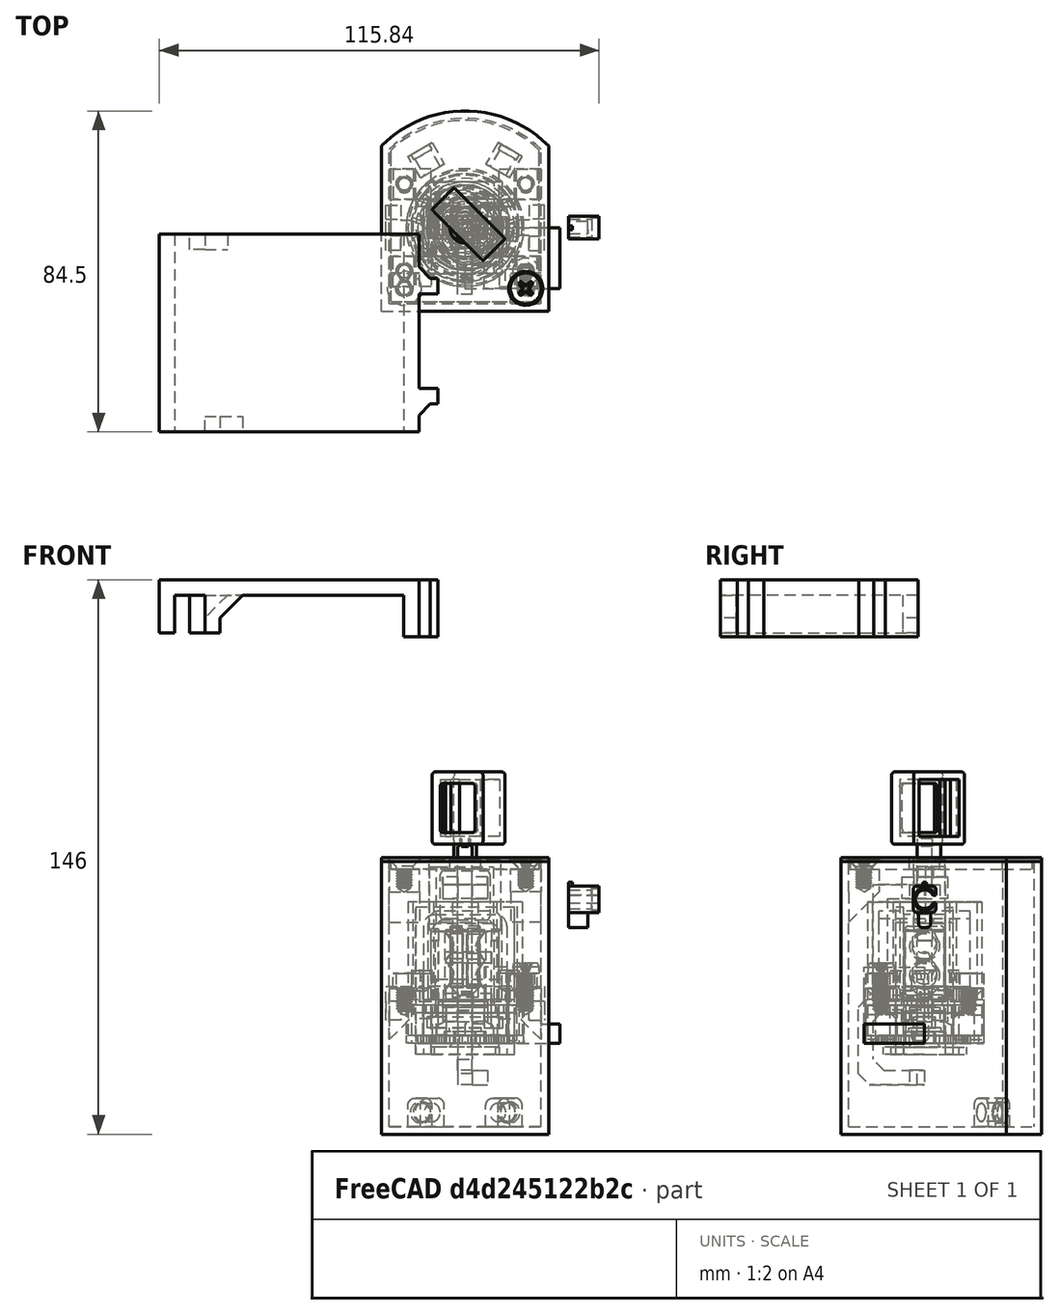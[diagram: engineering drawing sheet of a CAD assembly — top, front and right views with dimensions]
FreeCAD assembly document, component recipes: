
FREECAD ASSEMBLY — COMPONENT RECIPES ("laser2-1mm")

This assembly document has 31 components, labeled P0..P30 below (a component is one placed body or linked part). 31 of them carry a construction recipe — the FreeCAD feature program that regenerates the part from scratch, quoted from this document or its linked companion documents; the rest are supplied as boundary geometry only. No exploded tour is included for this assembly.
NOTE — document 2 of 2 of this assembly tour. The two overview renders and the header above are repeated from document 1; the component sections below continue where the previous document stopped.
COMPONENT P21 — recipe-attached ("design6-container", modeled in this document).
Construction recipe (the document's own serialized feature program — sketch geometry with constraints, then the solid features built on it; lengths are millimeters unless a unit is written):

FEATURE [PartDesign::SubShapeBinder] Binder041
  BindCopyOnChange = 0
  BindMode = 0
  ClaimChildren = false
  Context = -> Body034 [Binder041.]
  Fuse = false
  MakeFace = true
  OffsetFill = false
  OffsetIntersection = false
  OffsetJoinType = 0
  OffsetOpenResult = false
  PartialLoad = false
  Refine = true
  Relative = true
  Support = -> [Assembly]
  _Version = 2
FEATURE [Sketcher::SketchObject] Sketch161
  ArcFitTolerance = 1e-06
  AttachmentOffset = pos=(0,0,9) rot=(0,0,1;0rad)
  AttachmentSupport = -> [Binder041]
  ExternalGeometry = -> [Binder041]
  ExternalTypes = [0,0,0]
  FullyConstrained = true
  MakeInternals = false
  MapMode = 5
  Placement = pos=(2.78355e-11,2.19082e-10,-22) rot=(1,0,0;3.14159rad)
  sketch-geometry (15):
    g0: LineSegment [constr] StartX=-20 StartY=28.7612 StartZ=0 EndX=-20 EndY=-28.7612 EndZ=0
    g1: LineSegment [constr] StartX=-20 StartY=-28.7612 StartZ=0 EndX=20 EndY=-28.7612 EndZ=0
    g2: LineSegment [constr] StartX=20 StartY=-28.7612 StartZ=0 EndX=20 EndY=28.7612 EndZ=0
    g3: LineSegment [constr] StartX=20 StartY=28.7612 StartZ=0 EndX=-20 EndY=28.7612 EndZ=0
    g4: GeomPoint X=-1e-16 Y=28.7612 Z=0
    g5: GeomPoint X=1e-16 Y=-28.7612 Z=0
    g6: LineSegment StartX=-22 StartY=22 StartZ=0 EndX=-22 EndY=-21.5 EndZ=0
    g7: GeomPoint X=-1e-16 Y=30.7612 Z=0
    g8: LineSegment [constr] StartX=-1e-16 StartY=28.7612 StartZ=0 EndX=-1e-16 EndY=30.7612 EndZ=0
    g9: LineSegment StartX=22 StartY=22 StartZ=0 EndX=22 EndY=-21.5 EndZ=0
    g10: GeomPoint X=0 Y=-30.7612 Z=0
    g11: ArcOfCircle CenterX=0 CenterY=0 CenterZ=0 NormalX=0 NormalY=0 NormalZ=1 AngleXU=0 Radius=30.7612 StartAngle=3.9155 EndAngle=5.50928
    g12: LineSegment StartX=-22 StartY=22 StartZ=0 EndX=22 EndY=22 EndZ=0
    g13: LineSegment [constr] StartX=-19 StartY=-15.5 StartZ=0 EndX=-22 EndY=-15.5 EndZ=0
    g14: LineSegment [constr] StartX=-22 StartY=-21.5 StartZ=0 EndX=-22 EndY=-15.5 EndZ=0
  constraints (36):
    c: Coincident(g0,g1)
    c: Coincident(g1,g2)
    c: Coincident(g2,g3)
    c: Coincident(g3,g0)
    c: Vertical(g0)
    c: Vertical(g2)
    c: Horizontal(g1)
    c: Horizontal(g3)
    c: Symmetric(g3,g3,g4)
    c: Symmetric(g1,g1,g5)
    c: Symmetric(g5,g4,g-1)
    c: Vertical(g6)
    c: Distance(g6,g0) = 2
    c: Coincident(g8,g4)
    c: Coincident(g8,g7)
    c: Distance(g8,g8) = 2
    c: Vertical(g8)
    c: Vertical(g9)
    c: Distance(g2,g9) = 2
    c: PointOnObject(g10,g-2)
    c: Distance(g10,g5) = 2
    c: Coincident(g11,g-1)
    c: Coincident(g11,g6)
    c: Coincident(g11,g9)
    c: PointOnObject(g10,g11)
    c: Coincident(g12,g6)
    c: Coincident(g12,g9)
    c: Horizontal(g12)
    c: Distance(g-3,g0) = 1
    c: Coincident(g13,g-5)
    c: PointOnObject(g13,g6)
    c: Horizontal(g13)
    c: Distance(g-4,g12) = 4.5
    c: Coincident(g14,g6)
    c: Coincident(g14,g13)
    c: Distance(g14,g14) = 6
FEATURE [PartDesign::Pad] Pad109
  Direction = (1.2653e-12,9.9583e-12,-1)
  Length = 2
  Length2 = 10
  Profile = -> Sketch161
  ReferenceAxis = -> Sketch161 [N_Axis]
  Refine = true
  SideType = 0
  Suppressed = false
  Type = 0
  Type2 = 0
FEATURE [Sketcher::SketchObject] Sketch162
  ArcFitTolerance = 1e-06
  AttachmentSupport = -> [Pad109]
  ExternalGeometry = -> [Pad109]
  ExternalTypes = [0]
  FullyConstrained = true
  MakeInternals = false
  MapMode = 5
  Placement = pos=(2.78354e-11,2.19082e-10,-22) rot=(0,0,1;0rad)
  sketch-geometry (8):
    g0: LineSegment StartX=20 StartY=-20 StartZ=0 EndX=20 EndY=20.6689 EndZ=0
    g1: ArcOfCircle CenterX=1e-16 CenterY=-4e-16 CenterZ=0 NormalX=0 NormalY=0 NormalZ=1 AngleXU=0 Radius=28.7612 StartAngle=0.801845 EndAngle=2.33975
    g2: LineSegment StartX=-20 StartY=-20 StartZ=0 EndX=-20 EndY=20.6689 EndZ=0
    g3: LineSegment StartX=-20 StartY=-20 StartZ=0 EndX=20 EndY=-20 EndZ=0
    g4: LineSegment [constr] StartX=0 StartY=28.7612 StartZ=0 EndX=0 EndY=30.7612 EndZ=0
    g5: GeomPoint [constr] X=0 Y=20.6689 Z=0
    g6: LineSegment [constr] StartX=-20 StartY=20.6689 StartZ=0 EndX=0 EndY=20.6689 EndZ=0
    g7: LineSegment [constr] StartX=0 StartY=20.6689 StartZ=0 EndX=20 EndY=20.6689 EndZ=0
  constraints (22):
    c: Coincident(g0,g1)
    c: Coincident(g0,g3)
    c: Coincident(g1,g2)
    c: Coincident(g2,g3)
    c: Distance(g-5,g0) = 2
    c: Distance(g0,g-6) = 2
    c: Distance(g2,g-3) = 2
    c: Distance(g1,g-3) = 2
    c: Distance(g0,g-5) = 2
    c: PointOnObject(g4,g1)
    c: PointOnObject(g4,g-4)
    c: Vertical(g4)
    c: Distance(g4,g4) = 2
    c: PointOnObject(g4,g-2)
    c: PointOnObject(g5,g-2)
    c: Coincident(g6,g1)
    c: Coincident(g6,g5)
    c: Horizontal(g6)
    c: Coincident(g7,g5)
    c: Coincident(g7,g0)
    c: Coincident(g1,g-4)
    c: Distance(g2,g-6) = 2
FEATURE [PartDesign::Pad] Pad110
  BaseFeature = -> Pad109
  Direction = (-1.2652e-12,-9.9583e-12,1)
  Length = 10
  Length2 = 10
  Offset = -4
  Profile = -> Sketch162
  ReferenceAxis = -> Sketch162 [N_Axis]
  Refine = true
  SideType = 0
  Suppressed = false
  Type = 3
  Type2 = 0
  UpToFace = -> Binder041 [Face166]
FEATURE [Sketcher::SketchObject] Sketch176
  ArcFitTolerance = 1e-06
  AttachmentSupport = -> [Pad110]
  ExternalGeometry = -> [Binder041]
  ExternalTypes = [0,0,0,0]
  FullyConstrained = true
  MakeInternals = false
  MapMode = 5
  Placement = pos=(20,0,2.53049e-11) rot=(0.57735,-0.57735,-0.57735;2.0944rad)
  sketch-geometry (4):
    g0: LineSegment StartX=7.5 StartY=14.4 StartZ=0 EndX=7.5 EndY=7.4 EndZ=0
    g1: LineSegment StartX=7.5 StartY=7.4 StartZ=0 EndX=15.5 EndY=7.4 EndZ=0
    g2: LineSegment StartX=15.5 StartY=7.4 StartZ=0 EndX=15.5 EndY=14.4 EndZ=0
    g3: LineSegment StartX=15.5 StartY=14.4 StartZ=0 EndX=7.5 EndY=14.4 EndZ=0
  constraints (10):
    c: Coincident(g0,g1)
    c: Coincident(g1,g2)
    c: Coincident(g2,g3)
    c: Coincident(g3,g0)
    c: Vertical(g0)
    c: Vertical(g2)
    c: Horizontal(g1)
    c: Coincident(g0,g-5)
    c: Coincident(g2,g-6)
    c: DistanceY(g2,g2) = 7
FEATURE [PartDesign::Pad] Pad118
  BaseFeature = -> Pad110
  Direction = (-1,0,-1.2652e-12)
  Length = 6
  Length2 = 10
  Offset = -0.5
  Profile = -> Sketch176
  ReferenceAxis = -> Sketch176 [N_Axis]
  Refine = true
  SideType = 0
  Suppressed = false
  Type = 3
  Type2 = 0
  UpToFace = -> Binder041 [Face41]
FEATURE [Sketcher::SketchObject] Sketch177
  ArcFitTolerance = 1e-06
  AttachmentSupport = -> [Pad118]
  ExternalGeometry = -> [Binder041]
  ExternalTypes = [0]
  FullyConstrained = true
  MakeInternals = false
  MapMode = 5
  Placement = pos=(-1.8219e-11,-1.9345e-12,14.4) rot=(0,0,1;0rad)
  sketch-geometry (1):
    g0: GeomPoint X=16 Y=-11.5 Z=0
  constraints (1):
    c: Coincident(g0,g-3)
FEATURE [PartDesign::Chamfer] Chamfer009
  Angle = 45
  Base = -> Pad118 [Edge21]
  BaseFeature = -> Pad118
  ChamferType = 2
  FlipDirection = false
  Refine = true
  Size = 6.49
  Size2 = 1
  SupportTransform = false
  Suppressed = false
  UseAllEdges = false
FEATURE [PartDesign::Hole] Hole
  BaseFeature = -> Chamfer009
  BaseProfileType = 7
  CustomThreadClearance = 0
  Depth = 6
  DepthType = 0
  Diameter = 3.322
  DrillForDepth = false
  DrillPoint = 1
  DrillPointAngle = 118
  HoleCutCountersinkAngle = 90
  HoleCutCustomValues = false
  HoleCutDepth = 0
  HoleCutDiameter = 0
  HoleCutType = 0
  ModelThread = true
  Profile = -> Sketch177 [Vertex1]
  Refine = true
  Suppressed = false
  Tapered = false
  TaperedAngle = 90
  ThreadClass = 0
  ThreadDepth = 6
  ThreadDepthType = 0
  ThreadDiameter = 4
  ThreadDirection = 0
  ThreadFit = 0
  ThreadSize = 11
  ThreadType = 1
  Threaded = true
  UseCustomThreadClearance = false
FEATURE [PartDesign::Mirrored] Mirror014
  MirrorPlane = -> YZ_Plane035
  Refine = true
  Suppressed = false
  TransformMode = 0
FEATURE [PartDesign::Mirrored] Mirror015
  MirrorPlane = -> XZ_Plane035
  Refine = true
  Suppressed = false
  TransformMode = 0
FEATURE [PartDesign::MultiTransform] MultiTransform006
  BaseFeature = -> Hole
  Originals = -> [Pad118,Chamfer009,Hole]
  Refine = true
  Suppressed = false
  TransformMode = 0
  Transformations = -> [Mirror014,Mirror015]
FEATURE [Sketcher::SketchObject] Sketch178
  ArcFitTolerance = 1e-06
  AttachmentSupport = -> [MultiTransform006]
  ExternalGeometry = -> [MultiTransform006]
  ExternalTypes = [0,0]
  FullyConstrained = true
  MakeInternals = false
  MapMode = 5
  Placement = pos=(1.8e-15,-20,-1.99166e-10) rot=(0,0.707107,0.707107;3.14159rad)
  sketch-geometry (4):
    g0: LineSegment StartX=-20 StartY=45.8 StartZ=0 EndX=-20 EndY=39.8 EndZ=0
    g1: LineSegment StartX=-20 StartY=39.8 StartZ=0 EndX=-12 EndY=39.8 EndZ=0
    g2: LineSegment StartX=-12 StartY=39.8 StartZ=0 EndX=-12 EndY=45.8 EndZ=0
    g3: LineSegment StartX=-12 StartY=45.8 StartZ=0 EndX=-20 EndY=45.8 EndZ=0
  constraints (12):
    c: Coincident(g0,g1)
    c: Coincident(g1,g2)
    c: Coincident(g2,g3)
    c: Coincident(g3,g0)
    c: Vertical(g0)
    c: Vertical(g2)
    c: Horizontal(g1)
    c: Horizontal(g3)
    c: Distance(g0,g2) = 8
    c: Distance(g1,g3) = 6
    c: PointOnObject(g0,g-3)
    c: Distance(g0,g-3) = 2
FEATURE [PartDesign::Pad] Pad119
  BaseFeature = -> MultiTransform006
  Direction = (0,1,9.9583e-12)
  Length = 8
  Length2 = 10
  Profile = -> Sketch178
  ReferenceAxis = -> Sketch178 [N_Axis]
  Refine = true
  SideType = 0
  Suppressed = false
  Type = 0
  Type2 = 0
FEATURE [PartDesign::Chamfer] Chamfer010
  Angle = 45
  Base = -> Pad119 [Edge32]
  BaseFeature = -> Pad119
  ChamferType = 2
  FlipDirection = false
  Refine = true
  Size = 7.99
  Size2 = 1
  SupportTransform = false
  Suppressed = false
  UseAllEdges = false
FEATURE [Sketcher::SketchObject] Sketch179
  ArcFitTolerance = 1e-06
  AttachmentSupport = -> [Chamfer010]
  ExternalGeometry = -> [Chamfer010]
  ExternalTypes = [0,0]
  FullyConstrained = true
  MakeInternals = false
  MapMode = 5
  Placement = pos=(0,-4.56091e-10,45.8) rot=(0,0,1;0rad)
  sketch-geometry (2):
    g0: LineSegment [constr] StartX=12 StartY=-12 StartZ=0 EndX=20 EndY=-20 EndZ=0
    g1: GeomPoint X=16 Y=-16 Z=0
  constraints (3):
    c: Coincident(g0,g-6)
    c: Coincident(g0,g-5)
    c: Symmetric(g0,g0,g1)
FEATURE [PartDesign::Hole] Hole004
  BaseFeature = -> Chamfer010
  BaseProfileType = 7
  CustomThreadClearance = 0
  Depth = 5
  DepthType = 0
  Diameter = 3.322
  DrillForDepth = false
  DrillPoint = 1
  DrillPointAngle = 118
  HoleCutCountersinkAngle = 90
  HoleCutCustomValues = false
  HoleCutDepth = 0
  HoleCutDiameter = 0
  HoleCutType = 0
  ModelThread = true
  Profile = -> Sketch179 [Vertex1]
  Refine = true
  Suppressed = false
  Tapered = false
  TaperedAngle = 90
  ThreadClass = 0
  ThreadDepth = 5
  ThreadDepthType = 0
  ThreadDiameter = 4
  ThreadDirection = 0
  ThreadFit = 0
  ThreadSize = 11
  ThreadType = 1
  Threaded = true
  UseCustomThreadClearance = false
FEATURE [PartDesign::Mirrored] Mirrored007
  BaseFeature = -> Hole004
  MirrorPlane = -> YZ_Plane035
  Originals = -> [Pad119,Chamfer010,Hole004]
  Refine = true
  Suppressed = false
  TransformMode = 0
FEATURE [Sketcher::SketchObject] Sketch185
  ArcFitTolerance = 1e-06
  AttachmentSupport = -> [Mirrored007]
  ExternalGeometry = -> [Mirrored007]
  ExternalTypes = [0]
  FullyConstrained = true
  MakeInternals = false
  MapMode = 5
  Placement = pos=(2.78354e-11,2.19082e-10,-22) rot=(0,0,1;0rad)
  expr: Constraints[0] = 90 - 30
  expr: Constraints[18] = 4.8 mm + 2.5 mm
  expr: Constraints[19] = 5.5 mm + 1 mm
  expr: Constraints[4] = 90 + 30
  sketch-geometry (14):
    g0: LineSegment [constr] StartX=0 StartY=0 StartZ=0 EndX=14.3806 EndY=24.9079 EndZ=0
    g1: LineSegment [constr] StartX=0 StartY=0 StartZ=0 EndX=-14.3806 EndY=24.9079 EndZ=0
    g2: LineSegment StartX=-11.7916 StartY=13.1236 StartZ=0 EndX=-5.4696 EndY=16.7736 EndZ=0
    g3: LineSegment StartX=-11.7916 StartY=13.1236 StartZ=0 EndX=-15.0416 EndY=18.7528 EndZ=0
    g4: LineSegment StartX=-15.0416 StartY=18.7528 StartZ=0 EndX=-8.7196 EndY=22.4028 EndZ=0
    g5: LineSegment StartX=-8.7196 StartY=22.4028 StartZ=0 EndX=-5.4696 EndY=16.7736 EndZ=0
    g6: LineSegment [constr] StartX=-15.0416 StartY=18.7528 StartZ=0 EndX=-5.4696 EndY=16.7736 EndZ=0
    g7: GeomPoint [constr] X=-10.2556 Y=17.7632 Z=0
    g8: LineSegment StartX=5.4696 StartY=16.7736 StartZ=0 EndX=11.7916 EndY=13.1236 EndZ=0
    g9: LineSegment StartX=11.7916 StartY=13.1236 StartZ=0 EndX=15.0416 EndY=18.7528 EndZ=0
    g10: LineSegment StartX=15.0416 StartY=18.7528 StartZ=0 EndX=8.7196 EndY=22.4028 EndZ=0
    g11: LineSegment StartX=8.7196 StartY=22.4028 StartZ=0 EndX=5.4696 EndY=16.7736 EndZ=0
    g12: LineSegment [constr] StartX=11.7916 StartY=13.1236 StartZ=0 EndX=8.7196 EndY=22.4028 EndZ=0
    g13: GeomPoint [constr] X=10.2556 Y=17.7632 Z=0
  constraints (36):
    c: Angle(g-1,g0) = 1.0472
    c: Coincident(g0,g-1)
    c: PointOnObject(g0,g-3)
    c: Coincident(g1,g0)
    c: Angle(g-1,g1) = 2.0944
    c: PointOnObject(g1,g-3)
    c: Coincident(g3,g2)
    c: Coincident(g5,g4)
    c: Coincident(g5,g2)
    c: Perpendicular(g4,g1)
    c: Perpendicular(g2,g1)
    c: Parallel(g5,g3)
    c: Parallel(g3,g1)
    c: Coincident(g4,g3)
    c: Coincident(g6,g3)
    c: Coincident(g6,g2)
    c: Symmetric(g6,g6,g7)
    c: PointOnObject(g7,g1)
    c: Distance(g2,g2) = 7.3
    c: Distance(g5,g5) = 6.5
    c: Distance(g1,g4) = 5
    c: Coincident(g10,g9)
    c: Coincident(g11,g8)
    c: Parallel(g11,g9)
    c: Parallel(g9,g0)
    c: Perpendicular(g0,g8)
    c: Perpendicular(g10,g0)
    c: Coincident(g11,g10)
    c: Coincident(g9,g8)
    c: Distance(g0,g10) = 5
    c: Coincident(g12,g8)
    c: Coincident(g12,g10)
    c: Symmetric(g12,g12,g13)
    c: PointOnObject(g13,g0)
    c: Equal(g8,g2)
    c: Equal(g11,g5)
FEATURE [PartDesign::Pad] Pad122
  BaseFeature = -> Mirrored007
  Direction = (-1.2652e-12,-9.9583e-12,1)
  Length = 7.5
  Length2 = 10
  Profile = -> Sketch185
  ReferenceAxis = -> Sketch185 [N_Axis]
  Refine = true
  SideType = 0
  Suppressed = false
  Type = 0
  Type2 = 0
FEATURE [Sketcher::SketchObject] Sketch186
  ArcFitTolerance = 1e-06
  AttachmentSupport = -> [Pad122]
  ExternalGeometry = -> [Pad122]
  ExternalTypes = [0]
  FullyConstrained = true
  MakeInternals = false
  MapMode = 5
  Placement = pos=(-8.63059,14.9486,1.37943e-10) rot=(0.935113,0.250563,0.250563;1.63783rad)
  sketch-geometry (3):
    g0: LineSegment [constr] StartX=3.65 StartY=-22 StartZ=0 EndX=-3.65 EndY=-14.5 EndZ=0
    g1: GeomPoint [constr] X=2.67475e-11 Y=-18.25 Z=0
    g2: Circle CenterX=2.67475e-11 CenterY=-18.25 CenterZ=0 NormalX=0 NormalY=0 NormalZ=1 AngleXU=0 Radius=2.4
  constraints (5):
    c: Coincident(g0,g-5)
    c: Coincident(g0,g-6)
    c: Symmetric(g0,g0,g1)
    c: Diameter(g2) = 4.8
    c: Coincident(g2,g1)
FEATURE [PartDesign::Pocket] Pocket036
  BaseFeature = -> Pad122
  Direction = (-0.5,0.866025,7.9912e-12)
  Length = 5
  Length2 = 5
  Profile = -> Sketch186
  ReferenceAxis = -> Sketch186 [N_Axis]
  Refine = true
  SideType = 0
  Suppressed = false
  Type = 0
  Type2 = 0
FEATURE [Sketcher::SketchObject] Sketch187
  ArcFitTolerance = 1e-06
  AttachmentSupport = -> [Pocket036]
  ExternalGeometry = -> [Pocket036]
  ExternalTypes = [0]
  FullyConstrained = true
  MakeInternals = false
  MapMode = 5
  Placement = pos=(-11.8806,20.5778,1.89887e-10) rot=(-0.186157,0.694747,0.694747;3.50969rad)
  sketch-geometry (3):
    g0: LineSegment [constr] StartX=-3.65 StartY=-14.5 StartZ=0 EndX=3.65 EndY=-22 EndZ=0
    g1: GeomPoint [constr] X=-2.67905e-11 Y=-18.25 Z=0
    g2: Circle CenterX=-2.67905e-11 CenterY=-18.25 CenterZ=0 NormalX=0 NormalY=0 NormalZ=1 AngleXU=0 Radius=2.8
  constraints (5):
    c: Coincident(g0,g-6)
    c: Coincident(g0,g-5)
    c: Symmetric(g0,g0,g1)
    c: Diameter(g2) = 5.6
    c: Coincident(g2,g1)
FEATURE [PartDesign::Pocket] Pocket037
  BaseFeature = -> Pocket036
  Direction = (0.5,-0.866025,-7.9914e-12)
  Length = 1.5
  Length2 = 5
  Profile = -> Sketch187
  ReferenceAxis = -> Sketch187 [N_Axis]
  Refine = true
  SideType = 0
  Suppressed = false
  Type = 0
  Type2 = 0
FEATURE [Sketcher::SketchObject] Sketch188
  ArcFitTolerance = 1e-06
  AttachmentSupport = -> [Pocket037]
  ExternalGeometry = -> [Pocket037]
  ExternalTypes = [0]
  FullyConstrained = true
  MakeInternals = false
  MapMode = 5
  Placement = pos=(8.63059,14.9486,1.59782e-10) rot=(0.935113,-0.250563,-0.250563;1.63783rad)
  sketch-geometry (3):
    g0: LineSegment [constr] StartX=-3.65 StartY=-14.5 StartZ=0 EndX=3.65 EndY=-22 EndZ=0
    g1: GeomPoint [constr] X=2.66088e-11 Y=-18.25 Z=0
    g2: Circle CenterX=2.66088e-11 CenterY=-18.25 CenterZ=0 NormalX=0 NormalY=0 NormalZ=1 AngleXU=0 Radius=2.4
  constraints (5):
    c: Coincident(g0,g-6)
    c: Coincident(g0,g-5)
    c: Symmetric(g0,g0,g1)
    c: Diameter(g2) = 4.8
    c: Coincident(g2,g1)
FEATURE [PartDesign::Pocket] Pocket038
  BaseFeature = -> Pocket037
  Direction = (0.5,0.866025,9.2567e-12)
  Length = 5
  Length2 = 5
  Profile = -> Sketch188
  ReferenceAxis = -> Sketch188 [N_Axis]
  Refine = true
  SideType = 0
  Suppressed = false
  Type = 0
  Type2 = 0
FEATURE [Sketcher::SketchObject] Sketch189
  ArcFitTolerance = 1e-06
  AttachmentSupport = -> [Pocket038]
  ExternalGeometry = -> [Pocket038]
  ExternalTypes = [0]
  FullyConstrained = true
  MakeInternals = false
  MapMode = 5
  Placement = pos=(11.8806,20.5778,2.19951e-10) rot=(0.186157,0.694747,0.694747;2.77349rad)
  sketch-geometry (3):
    g0: LineSegment [constr] StartX=3.65 StartY=-22 StartZ=0 EndX=-3.65 EndY=-14.5 EndZ=0
    g1: GeomPoint [constr] X=-2.66087e-11 Y=-18.25 Z=0
    g2: Circle CenterX=-2.66087e-11 CenterY=-18.25 CenterZ=0 NormalX=0 NormalY=0 NormalZ=1 AngleXU=0 Radius=2.8
  constraints (5):
    c: Coincident(g0,g-5)
    c: Coincident(g0,g-6)
    c: Symmetric(g0,g0,g1)
    c: Diameter(g2) = 5.6
    c: Coincident(g2,g1)
FEATURE [PartDesign::Pocket] Pocket039
  BaseFeature = -> Pocket038
  Direction = (-0.5,-0.866025,-9.2567e-12)
  Length = 1.5
  Length2 = 5
  Profile = -> Sketch189
  ReferenceAxis = -> Sketch189 [N_Axis]
  Refine = true
  SideType = 0
  Suppressed = false
  Type = 0
  Type2 = 0
FEATURE [PartDesign::Fillet] Fillet024
  Base = -> Pocket039 [Edge152,Edge148,Edge142,Edge138]
  BaseFeature = -> Pocket039
  Radius = 2
  Refine = true
  SupportTransform = false
  Suppressed = false
  UseAllEdges = false
FEATURE [PartDesign::Body] Body034  label="design6-container"
  AllowCompound = false
  Group = -> [Binder041,Sketch161,Pad109,Sketch162,Pad110,Sketch176,Pad118,Chamfer009,Sketch177,Hole,MultiTransform006,Mirror014,Mirror015,Sketch178,Pad119,Chamfer010,Sketch179,Hole004,Mirrored007,Sketch185,Pad122,Sketch186,Pocket036,Sketch187,Pocket037,Sketch188,Pocket038,Sketch189,Pocket039,Fillet024]
  Origin = -> Origin075
  Tip = -> Fillet024
COMPONENT P22 — recipe-attached ("design6-container-lid", modeled in this document).
Construction recipe (the document's own serialized feature program — sketch geometry with constraints, then the solid features built on it; lengths are millimeters unless a unit is written):

FEATURE [PartDesign::SubShapeBinder] Binder042
  BindCopyOnChange = 0
  BindMode = 0
  ClaimChildren = false
  Context = -> Body037 [Binder042.]
  Fuse = false
  MakeFace = true
  OffsetFill = false
  OffsetIntersection = false
  OffsetJoinType = 0
  OffsetOpenResult = false
  PartialLoad = false
  Refine = true
  Relative = true
  Support = -> [Body034]
  _Version = 2
FEATURE [Sketcher::SketchObject] Sketch180
  ArcFitTolerance = 1e-06
  AttachmentSupport = -> [Binder042]
  ExternalGeometry = -> [Binder042]
  ExternalTypes = [0]
  FullyConstrained = false
  MakeInternals = false
  MapMode = 5
  Placement = pos=(0,-4.56091e-10,45.8) rot=(0,0,1;0rad)
  sketch-geometry (5):
    g0: LineSegment StartX=-19.5 StartY=-19.5 StartZ=0 EndX=19.5 EndY=-19.5 EndZ=0
    g1: LineSegment StartX=19.5 StartY=-19.5 StartZ=0 EndX=19.5 EndY=20.4559 EndZ=0
    g2: ArcOfCircle CenterX=2.78355e-11 CenterY=-1.1e-15 CenterZ=0 NormalX=-1.785e-13 NormalY=0 NormalZ=1 AngleXU=0 Radius=28.2612 StartAngle=0.809318 EndAngle=2.33228
    g3: LineSegment StartX=-19.5 StartY=-19.5 StartZ=0 EndX=-19.5 EndY=20.4559 EndZ=0
    g4: LineSegment [constr] StartX=0 StartY=28.2612 StartZ=0 EndX=0 EndY=28.7612 EndZ=0
FEATURE [PartDesign::Pad] Pad120
  Direction = (0,-9.9583e-12,1)
  Length = 10
  Length2 = 10
  Profile = -> Sketch180
  ReferenceAxis = -> Sketch180 [N_Axis]
  Refine = true
  SideType = 0
  Suppressed = false
  Type = 3
  Type2 = 0
  UpToFace = -> Binder042 [Face23]
FEATURE [Sketcher::SketchObject] Sketch181
  ArcFitTolerance = 1e-06
  AttachmentSupport = -> [Pad120]
  ExternalGeometry = -> [Binder042]
  ExternalTypes = [0,0,0,0]
  FullyConstrained = true
  MakeInternals = false
  MapMode = 5
  Placement = pos=(-1.56588e-08,2.32709e-10,47.8) rot=(0,0,1;0rad)
FEATURE [PartDesign::Pad] Pad121
  BaseFeature = -> Pad120
  Direction = (-3.27589e-10,4.8684e-12,1)
  Length = 1
  Length2 = 10
  Profile = -> Sketch181
  ReferenceAxis = -> Sketch181 [N_Axis]
  Refine = true
  SideType = 0
  Suppressed = false
  Type = 0
  Type2 = 0
FEATURE [Sketcher::SketchObject] Sketch183
  ArcFitTolerance = 1e-06
  AttachmentSupport = -> [Pad121]
  ExternalTypes = [0]
  FullyConstrained = true
  MakeInternals = false
  MapMode = 5
  Placement = pos=(-1.38313e-08,-1.11061e-11,48.8) rot=(0,0,1;0rad)
  sketch-geometry (1):
    g0: Circle CenterX=0 CenterY=0 CenterZ=0 NormalX=0 NormalY=0 NormalZ=1 AngleXU=0 Radius=4
  constraints (2):
    c: Diameter(g0) = 8
    c: Coincident(g0,g-1)
FEATURE [PartDesign::Pocket] Pocket035
  BaseFeature = -> Pad121
  Direction = (2.83428e-10,2.276e-13,-1)
  Length = 5
  Length2 = 5
  Profile = -> Sketch183
  ReferenceAxis = -> Sketch183 [N_Axis]
  Refine = true
  SideType = 0
  Suppressed = false
  Type = 1
  Type2 = 0
FEATURE [Sketcher::SketchObject] Sketch184
  ArcFitTolerance = 1e-06
  AttachmentSupport = -> [Pocket035]
  ExternalGeometry = -> [Binder042]
  ExternalTypes = [0,0]
  FullyConstrained = true
  MakeInternals = false
  MapMode = 5
  Placement = pos=(-1.38313e-08,-1.11061e-11,48.8) rot=(0,0,1;0rad)
  sketch-geometry (2):
    g0: GeomPoint X=16 Y=-16 Z=0
    g1: GeomPoint X=-16 Y=-16 Z=0
  constraints (2):
    c: Coincident(g0,g-4)
    c: Coincident(g1,g-3)
FEATURE [PartDesign::Hole] Hole005
  BaseFeature = -> Pocket035
  BaseProfileType = 7
  CustomThreadClearance = 0
  Depth = 25
  DepthType = 0
  Diameter = 4.5
  DrillForDepth = false
  DrillPoint = 1
  DrillPointAngle = 118
  HoleCutCountersinkAngle = 90
  HoleCutCustomValues = false
  HoleCutDepth = 4.5
  HoleCutDiameter = 9
  HoleCutType = 2
  ModelThread = false
  Profile = -> Sketch184 [Vertex1,Vertex2]
  Refine = true
  Suppressed = false
  Tapered = false
  TaperedAngle = 90
  ThreadClass = 0
  ThreadDepth = 25
  ThreadDepthType = 0
  ThreadDiameter = 4
  ThreadDirection = 0
  ThreadFit = 0
  ThreadSize = 11
  ThreadType = 1
  Threaded = false
  UseCustomThreadClearance = false
FEATURE [PartDesign::Body] Body037  label="design6-container-lid"
  AllowCompound = false
  Group = -> [Binder042,Sketch180,Pad120,Sketch181,Pad121,Sketch183,Pocket035,Sketch184,Hole005]
  Origin = -> Origin081
  Tip = -> Hole005
COMPONENT P23 — recipe-attached ("design6-rotor001", modeled in this document).
Construction recipe (the document's own serialized feature program — sketch geometry with constraints, then the solid features built on it; lengths are millimeters unless a unit is written):

FEATURE [PartDesign::SubShapeBinder] Binder035
  BindCopyOnChange = 0
  BindMode = 0
  ClaimChildren = false
  Context = -> Body030 [Binder035.]
  Fuse = false
  MakeFace = true
  OffsetFill = false
  OffsetIntersection = false
  OffsetJoinType = 0
  OffsetOpenResult = false
  PartialLoad = false
  Refine = true
  Relative = true
  Support = -> [Body029]
  _Version = 2
FEATURE [Sketcher::SketchObject] Sketch134
  ArcFitTolerance = 1e-06
  AttachmentSupport = -> [Origin067]
  ExternalGeometry = -> [Binder035]
  ExternalTypes = [0]
  FullyConstrained = true
  MakeInternals = false
  MapMode = 5
  sketch-geometry (1):
    g0: Circle CenterX=0 CenterY=0 CenterZ=0 NormalX=0 NormalY=0 NormalZ=1 AngleXU=0 Radius=7.5
  constraints (2):
    c: Coincident(g0,g-3)
    c: Distance(g0,g-3) = 2
FEATURE [PartDesign::Pad] Pad088
  Direction = (0,0,1)
  Length = 10
  Length2 = 10
  Profile = -> Sketch134
  ReferenceAxis = -> Sketch134 [N_Axis]
  Refine = true
  SideType = 0
  Suppressed = false
  Type = 3
  Type2 = 0
  UpToFace = -> Binder035 [Face3]
FEATURE [Sketcher::SketchObject] Sketch135
  ArcFitTolerance = 1e-06
  AttachmentSupport = -> [Pad088]
  ExternalGeometry = -> [Pad088]
  ExternalTypes = [0]
  FullyConstrained = true
  MakeInternals = false
  MapMode = 5
  Placement = pos=(0,0,3) rot=(0,0,1;0rad)
  sketch-geometry (1):
    g0: Circle CenterX=0 CenterY=0 CenterZ=0 NormalX=0 NormalY=0 NormalZ=1 AngleXU=0 Radius=4.25
  constraints (2):
    c: Diameter(g0) = 8.5
    c: Coincident(g0,g-1)
FEATURE [PartDesign::Pad] Pad089
  BaseFeature = -> Pad088
  Direction = (0,0,1)
  Length = 1
  Length2 = 10
  Profile = -> Sketch135
  ReferenceAxis = -> Sketch135 [N_Axis]
  Refine = true
  SideType = 0
  Suppressed = false
  Type = 0
  Type2 = 0
FEATURE [Sketcher::SketchObject] Sketch137
  ArcFitTolerance = 1e-06
  AttachmentSupport = -> [Pad089]
  ExternalGeometry = -> [Pad089]
  ExternalTypes = [0]
  FullyConstrained = true
  MakeInternals = false
  MapMode = 5
  Placement = pos=(0,0,4) rot=(0,0,1;0rad)
FEATURE [PartDesign::Pad] Pad090
  BaseFeature = -> Pad089
  Direction = (0,0,1)
  Length = 1
  Length2 = 10
  Profile = -> Sketch137
  ReferenceAxis = -> Sketch137 [N_Axis]
  Refine = true
  SideType = 0
  Suppressed = false
  Type = 0
  Type2 = 0
FEATURE [Sketcher::SketchObject] Sketch139
  ArcFitTolerance = 1e-06
  AttachmentSupport = -> [Pad090]
  ExternalTypes = [0]
  FullyConstrained = true
  MakeInternals = false
  MapMode = 5
  Placement = pos=(0,0,5) rot=(0,0,1;0rad)
  expr: Constraints[2] = VarSet.magnet_height + 0.2 mm
  expr: Constraints[4] = VarSet.magnet_diameter + 0.2 mm
  sketch-geometry (4):
    g0: LineSegment [constr] StartX=0.5 StartY=3.3 StartZ=0 EndX=0.5 EndY=-3.3 EndZ=0
    g1: LineSegment [constr] StartX=0.5 StartY=3.3 StartZ=0 EndX=3.9 EndY=3.3 EndZ=0
    g2: GeomPoint [constr] X=0.5 Y=0 Z=0
    g3: Circle CenterX=0 CenterY=0 CenterZ=0 NormalX=0 NormalY=0 NormalZ=1 AngleXU=0 Radius=5.10882
  constraints (11):
    c: Vertical(g0)
    c: Coincident(g1,g0)
    c: Distance(g1,g1) = 3.4
    c: Horizontal(g1)
    c: DistanceY(g0,g0) = 6.6
    c: Symmetric(g0,g0,g2)
    c: PointOnObject(g2,g-1)
    c: Distance(g-2,g0) = 0.5
    c: Coincident(g3,g-1)
    c: PointOnObject(g1,g3)
    c: Distance(g2,g3) = 4.60882  'PocketSize'
FEATURE [PartDesign::Pad] Pad091
  BaseFeature = -> Pad090
  Direction = (0,0,1)
  Length = 24.8
  Length2 = 10
  Profile = -> Sketch139
  ReferenceAxis = -> Sketch139 [N_Axis]
  Refine = true
  SideType = 0
  Suppressed = false
  Type = 0
  Type2 = 0
  expr: Length = 10 mm + 2 * VarSet.magnet_diameter + 2 mm
FEATURE [Part::DatumPlane] DatumPlane005
  AttachmentOffset = pos=(0,0,0) rot=(0.57735,0.57735,0.57735;2.0944rad)
  AttachmentSupport = -> [Pad091]
  MapMode = 47
  Placement = pos=(5.10882,0,29.8) rot=(0.57735,0.57735,0.57735;2.0944rad)
FEATURE [Sketcher::SketchObject] Sketch140
  ArcFitTolerance = 1e-06
  AttachmentSupport = -> [DatumPlane005]
  ExternalGeometry = -> [Pad091]
  ExternalTypes = [0]
  FullyConstrained = true
  MakeInternals = false
  MapMode = 5
  Placement = pos=(5.10882,0,29.8) rot=(0.57735,0.57735,0.57735;2.0944rad)
  expr: Constraints[3] = VarSet.magnet_diameter + 0.2 mm
  expr: Constraints[5] = VarSet.magnet_diameter + 0.2 mm
  sketch-geometry (5):
    g0: LineSegment [constr] StartX=-1.3e-15 StartY=0 StartZ=0 EndX=-1.3e-15 EndY=-24.8 EndZ=0
    g1: Circle CenterX=-4.55e-14 CenterY=-4.3 CenterZ=0 NormalX=0 NormalY=0 NormalZ=1 AngleXU=0 Radius=3.3
    g2: Circle CenterX=-1.118e-13 CenterY=-11.9 CenterZ=0 NormalX=0 NormalY=0 NormalZ=1 AngleXU=0 Radius=3.3
    g3: LineSegment [constr] StartX=-1.3e-15 StartY=-1 StartZ=0 EndX=-1.3e-15 EndY=0 EndZ=0
    g4: LineSegment [constr] StartX=-6.01e-14 StartY=-8.6 StartZ=0 EndX=-6.01e-14 EndY=-7.6 EndZ=0
  constraints (15):
    c: Coincident(g0,g-6)
    c: Coincident(g0,g-4)
    c: PointOnObject(g1,g0)
    c: Diameter(g1) = 6.6
    c: PointOnObject(g2,g0)
    c: Diameter(g2) = 6.6
    c: PointOnObject(g3,g1)
    c: Coincident(g3,g0)
    c: Vertical(g3)
    c: PointOnObject(g4,g2)
    c: PointOnObject(g4,g1)
    c: PointOnObject(g4,g0)
    c: Vertical(g4)
    c: Equal(g3,g4)
    c: Distance(g3,g3) = 1
FEATURE [PartDesign::Pocket] Pocket030
  BaseFeature = -> Pad091
  Direction = (-1,0,0)
  Length = 4.60882
  Length2 = 5
  Profile = -> Sketch140
  ReferenceAxis = -> Sketch140 [N_Axis]
  Refine = true
  SideType = 0
  Suppressed = false
  Type = 0
  Type2 = 0
  expr: Length = Sketch139.Constraints.PocketSize
FEATURE [PartDesign::Fillet] Fillet014
  Base = -> Pocket030 [Edge6,Edge13,Edge14,Edge12,Edge11,Edge8]
  BaseFeature = -> Pocket030
  Radius = 0.4
  Refine = true
  SupportTransform = false
  Suppressed = false
  UseAllEdges = false
FEATURE [PartDesign::Mirrored] Mirrored004
  BaseFeature = -> Fillet014
  MirrorPlane = -> YZ_Plane031
  Originals = -> [Fillet014,Pocket030]
  Refine = true
  Suppressed = false
  TransformMode = 0
FEATURE [PartDesign::Fillet] Fillet015
  Base = -> Mirrored004 [Edge30]
  BaseFeature = -> Mirrored004
  Radius = 1
  Refine = true
  SupportTransform = false
  Suppressed = false
  UseAllEdges = false
FEATURE [PartDesign::Fillet] Fillet017
  Base = -> Fillet015 [Edge2]
  BaseFeature = -> Fillet015
  Radius = 2
  Refine = true
  SupportTransform = false
  Suppressed = false
  UseAllEdges = false
FEATURE [Sketcher::SketchObject] Sketch146
  ArcFitTolerance = 1e-06
  AttachmentOffset = pos=(0,0,6) rot=(0,0,1;0rad)
  AttachmentSupport = -> [Origin067]
  ExternalGeometry = -> [Fillet017]
  ExternalTypes = [0,0]
  FullyConstrained = true
  MakeInternals = false
  MapMode = 5
  Placement = pos=(0,-6,1.3e-15) rot=(1,0,0;1.5708rad)
  sketch-geometry (8):
    g0: LineSegment StartX=-2.1 StartY=8.46879 StartZ=0 EndX=2.1 EndY=8.46879 EndZ=0
    g1: LineSegment StartX=2.1 StartY=8.46879 StartZ=0 EndX=2.1 EndY=12.6688 EndZ=0
    g2: LineSegment StartX=2.1 StartY=12.6688 StartZ=0 EndX=-2.1 EndY=12.6688 EndZ=0
    g3: LineSegment StartX=-2.1 StartY=12.6688 StartZ=0 EndX=-2.1 EndY=8.46879 EndZ=0
    g4: GeomPoint [constr] X=0 Y=10.5688 Z=0
    g5: LineSegment [constr] StartX=5.10882 StartY=14.2 StartZ=0 EndX=-3.05118 EndY=14.2 EndZ=0
    g6: LineSegment [constr] StartX=-2.1 StartY=12.6688 StartZ=0 EndX=-2.1 EndY=14.2 EndZ=0
    g7: LineSegment [constr] StartX=-2.1 StartY=8.46879 StartZ=0 EndX=-2.1 EndY=6.93757 EndZ=0
  constraints (22):
    c: Coincident(g0,g1)
    c: Coincident(g1,g2)
    c: Coincident(g2,g3)
    c: Coincident(g3,g0)
    c: Horizontal(g0)
    c: Horizontal(g2)
    c: Vertical(g1)
    c: Vertical(g3)
    c: Symmetric(g2,g0,g4)
    c: Distance(g1,g3) = 4.2
    c: Distance(g0,g2) = 4.2
    c: Horizontal(g5)
    c: PointOnObject(g4,g-2)
    c: Coincident(g5,g-4)
    c: Distance(g5,g5) = 8.16
    c: Coincident(g6,g2)
    c: PointOnObject(g6,g5)
    c: Vertical(g6)
    c: Coincident(g7,g0)
    c: PointOnObject(g7,g-3)
    c: Vertical(g7)
    c: Equal(g7,g6)
FEATURE [PartDesign::Pocket] Pocket031
  BaseFeature = -> Fillet017
  Direction = (0,1,0)
  Length = 5
  Length2 = 5
  Profile = -> Sketch146
  ReferenceAxis = -> Sketch146 [N_Axis]
  Refine = true
  SideType = 0
  Suppressed = false
  Type = 0
  Type2 = 0
FEATURE [PartDesign::Mirrored] Mirrored006
  BaseFeature = -> Pocket031
  MirrorPlane = -> XZ_Plane031
  Originals = -> [Pocket031]
  Refine = true
  Suppressed = false
  TransformMode = 0
FEATURE [Part::DatumPlane] DatumPlane006
  AttachmentOffset = pos=(0,0,0) rot=(0,1,0;0.785398rad)
  AttachmentSupport = -> [Origin067]
  MapMode = 5
  Placement = pos=(0,0,0) rot=(0.862856,0.357407,0.357407;1.71777rad)
FEATURE [PartDesign::Body] Body030  label="design6-rotor"
  AllowCompound = false
  Group = -> [Binder035,Sketch134,Pad088,Sketch135,Pad089,Sketch137,Pad090,Sketch139,Pad091,DatumPlane005,Sketch140,Pocket030,Fillet014,Mirrored004,Fillet015,Fillet017,Sketch146,Pocket031,DatumPlane006,Mirrored006]
  Origin = -> Origin067
  Tip = -> Mirrored006
COMPONENT P24 — recipe-attached ("design6-casing001", modeled in this document).
Construction recipe (the document's own serialized feature program — sketch geometry with constraints, then the solid features built on it; lengths are millimeters unless a unit is written):

FEATURE [PartDesign::SubShapeBinder] Binder036
  BindCopyOnChange = 0
  BindMode = 0
  ClaimChildren = false
  Context = -> Body031 [Binder036.]
  Fuse = false
  MakeFace = true
  OffsetFill = false
  OffsetIntersection = false
  OffsetJoinType = 0
  OffsetOpenResult = false
  PartialLoad = false
  Refine = true
  Relative = true
  Support = -> [Body030]
  _Version = 2
FEATURE [PartDesign::SubShapeBinder] Binder037
  BindCopyOnChange = 0
  BindMode = 0
  ClaimChildren = false
  Context = -> Body031 [Binder037.]
  Fuse = false
  MakeFace = true
  OffsetFill = false
  OffsetIntersection = false
  OffsetJoinType = 0
  OffsetOpenResult = false
  PartialLoad = false
  Refine = true
  Relative = true
  Support = -> [Body028]
  _Version = 2
FEATURE [Sketcher::SketchObject] Sketch141
  ArcFitTolerance = 1e-06
  AttachmentOffset = pos=(0,0,0) rot=(0,1,0;3.14159rad)
  AttachmentSupport = -> [Binder037]
  ExternalGeometry = -> [Binder037]
  ExternalTypes = [0,0]
  FullyConstrained = true
  MakeInternals = false
  MapMode = 5
  Placement = pos=(0,0,-3) rot=(0,0,1;3.14159rad)
  sketch-geometry (5):
    g0: LineSegment StartX=8.04674 StartY=7.5 StartZ=0 EndX=11 EndY=7.5 EndZ=0
    g1: LineSegment StartX=11 StartY=7.5 StartZ=0 EndX=11 EndY=-7.5 EndZ=0
    g2: LineSegment StartX=11 StartY=-7.5 StartZ=0 EndX=8.04674 EndY=-7.5 EndZ=0
    g3: GeomPoint X=11 Y=0 Z=0
    g4: ArcOfCircle CenterX=2e-16 CenterY=0 CenterZ=0 NormalX=0 NormalY=0 NormalZ=1 AngleXU=0 Radius=11 StartAngle=0.750245 EndAngle=5.53294
  constraints (13):
    c: Coincident(g1,g0)
    c: Vertical(g1)
    c: Coincident(g2,g1)
    c: Horizontal(g2)
    c: Horizontal(g0)
    c: Symmetric(g1,g1,g3)
    c: PointOnObject(g3,g-1)
    c: Distance(g1,g1) = 15
    c: Coincident(g4,g-3)
    c: Coincident(g4,g0)
    c: Coincident(g4,g2)
    c: Distance(g4,g-3) = 2
    c: Distance(g-3,g1) = 2
FEATURE [PartDesign::Pad] Pad092
  Direction = (1e-16,0,1)
  Length = 10
  Length2 = 10
  Profile = -> Sketch141
  ReferenceAxis = -> Sketch141 [N_Axis]
  Refine = true
  SideType = 0
  Suppressed = false
  Type = 3
  Type2 = 0
  UpToFace = -> Binder037 [Face4]
FEATURE [Sketcher::SketchObject] Sketch142
  ArcFitTolerance = 1e-06
  AttachmentSupport = -> [Pad092]
  ExternalGeometry = -> [Binder036,Pad092]
  ExternalTypes = [0,0,0,0,0,0]
  FullyConstrained = true
  MakeInternals = false
  MapMode = 5
  Placement = pos=(0,0,-1) rot=(0,0,1;0rad)
  sketch-geometry (5):
    g0: LineSegment StartX=-11 StartY=7.5 StartZ=0 EndX=-11 EndY=-7.5 EndZ=0
    g1: LineSegment StartX=-11 StartY=-7.5 StartZ=0 EndX=-9 EndY=-7.5 EndZ=0
    g2: LineSegment StartX=-9 StartY=-7.5 StartZ=0 EndX=-9 EndY=7.5 EndZ=0
    g3: LineSegment StartX=-9 StartY=7.5 StartZ=0 EndX=-11 EndY=7.5 EndZ=0
    g4: GeomPoint [constr] X=-9 Y=-8e-16 Z=0
  constraints (11):
    c: Coincident(g0,g1)
    c: Coincident(g3,g0)
    c: Vertical(g2)
    c: Horizontal(g1)
    c: Horizontal(g3)
    c: Coincident(g0,g-5)
    c: Coincident(g2,g3)
    c: Coincident(g2,g1)
    c: Coincident(g0,g-6)
    c: Symmetric(g2,g2,g4)
    c: PointOnObject(g4,g-8)
FEATURE [PartDesign::Pad] Pad093
  BaseFeature = -> Pad092
  Direction = (0,0,1)
  Length = 28
  Length2 = 10
  Offset = -4
  Profile = -> Sketch142
  ReferenceAxis = -> Sketch142 [N_Axis]
  Refine = true
  SideType = 0
  Suppressed = false
  Type = 3
  Type2 = 0
  UpToFace = -> Binder036 [Face8]
FEATURE [Sketcher::SketchObject] Sketch143
  ArcFitTolerance = 1e-06
  AttachmentSupport = -> [Pad093]
  ExternalGeometry = -> [Pad093]
  ExternalTypes = [0,0,0]
  FullyConstrained = true
  MakeInternals = false
  MapMode = 5
  Placement = pos=(-9,0,0) rot=(0.57735,0.57735,0.57735;2.0944rad)
  sketch-geometry (4):
    g0: LineSegment StartX=-7.5 StartY=33.8 StartZ=0 EndX=-7.5 EndY=31.8 EndZ=0
    g1: LineSegment StartX=-7.5 StartY=31.8 StartZ=0 EndX=7.5 EndY=31.8 EndZ=0
    g2: LineSegment StartX=7.5 StartY=31.8 StartZ=0 EndX=7.5 EndY=33.8 EndZ=0
    g3: LineSegment StartX=7.5 StartY=33.8 StartZ=0 EndX=-7.5 EndY=33.8 EndZ=0
  constraints (11):
    c: Coincident(g0,g1)
    c: Coincident(g1,g2)
    c: Coincident(g2,g3)
    c: Coincident(g3,g0)
    c: Vertical(g0)
    c: Vertical(g2)
    c: Horizontal(g1)
    c: Horizontal(g3)
    c: DistanceY(g2,g2) = 2
    c: PointOnObject(g0,g-4)
    c: Coincident(g2,g-5)
FEATURE [PartDesign::Pad] Pad094
  BaseFeature = -> Pad093
  Direction = (1,0,0)
  Length = 14
  Length2 = 10
  Profile = -> Sketch143
  ReferenceAxis = -> Sketch143 [N_Axis]
  Refine = true
  SideType = 0
  Suppressed = false
  Type = 0
  Type2 = 0
FEATURE [Sketcher::SketchObject] Sketch144
  ArcFitTolerance = 1e-06
  AttachmentSupport = -> [Pad094]
  ExternalGeometry = -> [Pad094]
  ExternalTypes = [0,0]
  FullyConstrained = true
  MakeInternals = false
  MapMode = 5
  Placement = pos=(-11,0,0) rot=(0.57735,-0.57735,-0.57735;2.0944rad)
  sketch-geometry (8):
    g0: LineSegment StartX=-7.5 StartY=33.8 StartZ=0 EndX=-7.5 EndY=-3 EndZ=0
    g1: LineSegment StartX=-7.5 StartY=-3 StartZ=0 EndX=-5.5 EndY=-3 EndZ=0
    g2: LineSegment StartX=-5.5 StartY=-3 StartZ=0 EndX=-5.5 EndY=33.8 EndZ=0
    g3: LineSegment StartX=-5.5 StartY=33.8 StartZ=0 EndX=-7.5 EndY=33.8 EndZ=0
    g4: LineSegment StartX=7.5 StartY=33.8 StartZ=0 EndX=5.5 EndY=33.8 EndZ=0
    g5: LineSegment StartX=5.5 StartY=33.8 StartZ=0 EndX=5.5 EndY=-3 EndZ=0
    g6: LineSegment StartX=5.5 StartY=-3 StartZ=0 EndX=7.5 EndY=-3 EndZ=0
    g7: LineSegment StartX=7.5 StartY=-3 StartZ=0 EndX=7.5 EndY=33.8 EndZ=0
  constraints (20):
    c: Coincident(g0,g1)
    c: Coincident(g1,g2)
    c: Coincident(g2,g3)
    c: Coincident(g3,g0)
    c: Vertical(g2)
    c: Horizontal(g1)
    c: Horizontal(g3)
    c: Distance(g1,g1) = 2
    c: Coincident(g4,g5)
    c: Coincident(g5,g6)
    c: Coincident(g6,g7)
    c: Coincident(g7,g4)
    c: Horizontal(g4)
    c: Horizontal(g6)
    c: Vertical(g5)
    c: Equal(g6,g1)
    c: Coincident(g0,g-3)
    c: Coincident(g0,g-3)
    c: Coincident(g4,g-4)
    c: Coincident(g-4,g6)
FEATURE [PartDesign::Pad] Pad095
  BaseFeature = -> Pad094
  Direction = (-1,0,0)
  Length = 2
  Length2 = 10
  Profile = -> Sketch144
  ReferenceAxis = -> Sketch144 [N_Axis]
  Refine = true
  SideType = 0
  Suppressed = false
  Type = 0
  Type2 = 0
FEATURE [Sketcher::SketchObject] Sketch145
  ArcFitTolerance = 1e-06
  AttachmentSupport = -> [Pad095]
  ExternalGeometry = -> [Pad095]
  ExternalTypes = [0,0,0,0,0,0]
  FullyConstrained = true
  MakeInternals = false
  MapMode = 5
  Placement = pos=(0,0,33.8) rot=(0,0,1;0rad)
  sketch-geometry (8):
    g0: LineSegment StartX=-13 StartY=-5.5 StartZ=0 EndX=-13 EndY=-7.5 EndZ=0
    g1: LineSegment StartX=-13 StartY=-7.5 StartZ=0 EndX=5 EndY=-7.5 EndZ=0
    g2: LineSegment StartX=5 StartY=-7.5 StartZ=0 EndX=5 EndY=-5.5 EndZ=0
    g3: LineSegment StartX=5 StartY=-5.5 StartZ=0 EndX=-13 EndY=-5.5 EndZ=0
    g4: LineSegment StartX=-13 StartY=5.5 StartZ=0 EndX=5 EndY=5.5 EndZ=0
    g5: LineSegment StartX=-13 StartY=5.5 StartZ=0 EndX=-13 EndY=7.5 EndZ=0
    g6: LineSegment StartX=-13 StartY=7.5 StartZ=0 EndX=5 EndY=7.5 EndZ=0
    g7: LineSegment StartX=5 StartY=7.5 StartZ=0 EndX=5 EndY=5.5 EndZ=0
  constraints (19):
    c: Coincident(g0,g1)
    c: Coincident(g1,g2)
    c: Coincident(g2,g3)
    c: Coincident(g3,g0)
    c: Vertical(g2)
    c: Horizontal(g1)
    c: Horizontal(g3)
    c: Coincident(g0,g-6)
    c: Horizontal(g4)
    c: PointOnObject(g1,g-7)
    c: Coincident(g0,g-6)
    c: Coincident(g4,g-4)
    c: Coincident(g5,g4)
    c: Coincident(g5,g-4)
    c: Coincident(g6,g5)
    c: Coincident(g6,g-7)
    c: Coincident(g7,g6)
    c: Coincident(g7,g4)
    c: PointOnObject(g4,g-7)
FEATURE [PartDesign::Pad] Pad096
  BaseFeature = -> Pad095
  Direction = (0,0,1)
  Length = 2
  Length2 = 10
  Profile = -> Sketch145
  ReferenceAxis = -> Sketch145 [N_Axis]
  Refine = true
  SideType = 0
  Suppressed = false
  Type = 0
  Type2 = 0
FEATURE [PartDesign::Mirrored] Mirrored005
  BaseFeature = -> Pad096
  MirrorPlane = -> Sketch145 [V_Axis]
  Originals = -> [Pad096,Pad092,Pad093,Pad094,Pad095]
  Refine = true
  Suppressed = false
  TransformMode = 0
FEATURE [PartDesign::Fillet] Fillet021
  Base = -> Mirrored005 [Edge40,Edge4,Edge55,Edge59]
  BaseFeature = -> Mirrored005
  Radius = 3
  Refine = true
  SupportTransform = false
  Suppressed = false
  UseAllEdges = false
FEATURE [Sketcher::SketchObject] Sketch173
  ArcFitTolerance = 1e-06
  AttachmentSupport = -> [Fillet021]
  ExternalGeometry = -> [Fillet021]
  ExternalTypes = [0,0]
  FullyConstrained = true
  MakeInternals = false
  MapMode = 5
  Placement = pos=(9.6e-15,-7.5,6.85e-14) rot=(1,0,0;1.5708rad)
  sketch-geometry (6):
    g0: GeomPoint [constr] X=13 Y=16.4 Z=0
    g1: LineSegment StartX=9 StartY=18.4 StartZ=0 EndX=9 EndY=14.4 EndZ=0
    g2: LineSegment StartX=9 StartY=14.4 StartZ=0 EndX=13 EndY=14.4 EndZ=0
    g3: LineSegment StartX=13 StartY=14.4 StartZ=0 EndX=13 EndY=18.4 EndZ=0
    g4: LineSegment StartX=13 StartY=18.4 StartZ=0 EndX=9 EndY=18.4 EndZ=0
    g5: GeomPoint X=13 Y=16.4 Z=0
  constraints (13):
    c: Symmetric(g-4,g-4,g0)
    c: Coincident(g1,g2)
    c: Coincident(g2,g3)
    c: Coincident(g3,g4)
    c: Coincident(g4,g1)
    c: Vertical(g1)
    c: Vertical(g3)
    c: Horizontal(g2)
    c: Horizontal(g4)
    c: PointOnObject(g1,g-3)
    c: Symmetric(g3,g3,g5)
    c: Coincident(g5,g0)
    c: DistanceY(g3,g3) = 4
FEATURE [PartDesign::Pad] Pad116
  BaseFeature = -> Fillet021
  Direction = (0,-1,0)
  Length = 8
  Length2 = 10
  Profile = -> Sketch173
  ReferenceAxis = -> Sketch173 [N_Axis]
  Refine = true
  SideType = 0
  Suppressed = false
  Type = 0
  Type2 = 0
FEATURE [Sketcher::SketchObject] Sketch174
  ArcFitTolerance = 1e-06
  AttachmentSupport = -> [Pad116]
  ExternalGeometry = -> [Pad116]
  ExternalTypes = [0,0,0]
  FullyConstrained = true
  MakeInternals = false
  MapMode = 5
  Placement = pos=(13,4.8e-15,0) rot=(0.57735,0.57735,0.57735;2.0944rad)
  sketch-geometry (4):
    g0: LineSegment StartX=-15.5 StartY=18.4 StartZ=0 EndX=-15.5 EndY=14.4 EndZ=0
    g1: LineSegment StartX=-15.5 StartY=14.4 StartZ=0 EndX=-7.5 EndY=14.4 EndZ=0
    g2: LineSegment StartX=-7.5 StartY=14.4 StartZ=0 EndX=-7.5 EndY=18.4 EndZ=0
    g3: LineSegment StartX=-7.5 StartY=18.4 StartZ=0 EndX=-15.5 EndY=18.4 EndZ=0
  constraints (10):
    c: Coincident(g0,g1)
    c: Coincident(g1,g2)
    c: Coincident(g2,g3)
    c: Coincident(g3,g0)
    c: Vertical(g0)
    c: Vertical(g2)
    c: Horizontal(g1)
    c: Horizontal(g3)
    c: Coincident(g0,g-4)
    c: Coincident(g1,g-5)
FEATURE [PartDesign::Pad] Pad117
  BaseFeature = -> Pad116
  Direction = (1,0,0)
  Length = 6
  Length2 = 10
  Profile = -> Sketch174
  ReferenceAxis = -> Sketch174 [N_Axis]
  Refine = true
  SideType = 0
  Suppressed = false
  Type = 0
  Type2 = 0
FEATURE [Sketcher::SketchObject] Sketch175
  ArcFitTolerance = 1e-06
  AttachmentSupport = -> [Pad117]
  ExternalGeometry = -> [Pad117]
  ExternalTypes = [0,0]
  FullyConstrained = true
  MakeInternals = false
  MapMode = 5
  Placement = pos=(4.75e-14,7.62e-14,18.4) rot=(0,0,1;0rad)
  sketch-geometry (2):
    g0: LineSegment [constr] StartX=13 StartY=-7.5 StartZ=0 EndX=19 EndY=-15.5 EndZ=0
    g1: GeomPoint X=16 Y=-11.5 Z=0
  constraints (3):
    c: Coincident(g0,g-4)
    c: Coincident(g0,g-3)
    c: Symmetric(g0,g0,g1)
FEATURE [PartDesign::Mirrored] Mirror012
  MirrorPlane = -> YZ_Plane032
  Refine = true
  Suppressed = false
  TransformMode = 0
FEATURE [PartDesign::Mirrored] Mirror013
  MirrorPlane = -> XZ_Plane032
  Refine = true
  Suppressed = false
  TransformMode = 0
FEATURE [PartDesign::Hole] Hole003
  BaseFeature = -> Pad117
  BaseProfileType = 7
  CustomThreadClearance = 0
  Depth = 114.833
  DepthType = 1
  Diameter = 4.5
  DrillForDepth = false
  DrillPoint = 1
  DrillPointAngle = 118
  HoleCutCountersinkAngle = 90
  HoleCutCustomValues = false
  HoleCutDepth = 0
  HoleCutDiameter = 0
  HoleCutType = 0
  ModelThread = false
  Profile = -> Sketch175 [Vertex1]
  Refine = true
  Suppressed = false
  Tapered = false
  TaperedAngle = 90
  ThreadClass = 0
  ThreadDepth = 114.833
  ThreadDepthType = 0
  ThreadDiameter = 4
  ThreadDirection = 0
  ThreadFit = 0
  ThreadSize = 11
  ThreadType = 1
  Threaded = false
  UseCustomThreadClearance = false
FEATURE [PartDesign::Chamfer] Chamfer008
  Angle = 45
  Base = -> Hole003 [Edge63]
  BaseFeature = -> Hole003
  ChamferType = 2
  FlipDirection = false
  Refine = true
  Size = 7.99
  Size2 = 1
  SupportTransform = false
  Suppressed = false
  UseAllEdges = false
FEATURE [PartDesign::MultiTransform] MultiTransform005
  BaseFeature = -> Chamfer008
  Originals = -> [Pad116,Pad117,Chamfer008,Hole003]
  Refine = true
  Suppressed = false
  TransformMode = 0
  Transformations = -> [Mirror012,Mirror013]
FEATURE [PartDesign::Body] Body031  label="design6-casing"
  AllowCompound = false
  Group = -> [Binder036,Binder037,Sketch141,Pad092,Sketch142,Pad093,Sketch143,Pad094,Sketch144,Pad095,Sketch145,Pad096,Mirrored005,Fillet021,Sketch173,Pad116,Sketch174,Pad117,Sketch175,Hole003,Chamfer008,MultiTransform005,Mirror012,Mirror013]
  Origin = -> Origin069
  Tip = -> MultiTransform005
COMPONENT P25 — recipe-attached ("design6-attachment001", modeled in this document).
Construction recipe (the document's own serialized feature program — sketch geometry with constraints, then the solid features built on it; lengths are millimeters unless a unit is written):

FEATURE [PartDesign::SubShapeBinder] Binder038
  BindCopyOnChange = 0
  BindMode = 0
  ClaimChildren = false
  Context = -> Body032 [Binder038.]
  Fuse = false
  MakeFace = true
  OffsetFill = false
  OffsetIntersection = false
  OffsetJoinType = 0
  OffsetOpenResult = false
  PartialLoad = false
  Refine = true
  Relative = true
  Support = -> [Body030]
  _Version = 2
FEATURE [PartDesign::SubShapeBinder] Binder039
  BindCopyOnChange = 0
  BindMode = 0
  ClaimChildren = false
  Context = -> Body032 [Binder039.]
  Fuse = false
  MakeFace = true
  OffsetFill = false
  OffsetIntersection = false
  OffsetJoinType = 0
  OffsetOpenResult = false
  PartialLoad = false
  Refine = true
  Relative = true
  Support = -> [Body031]
  _Version = 2
FEATURE [Sketcher::SketchObject] Sketch147
  ArcFitTolerance = 1e-06
  AttachmentSupport = -> [Binder038]
  ExternalGeometry = -> [Binder038]
  ExternalTypes = [0,0,0,0]
  FullyConstrained = true
  MakeInternals = false
  MapMode = 5
  Placement = pos=(0,-1,0) rot=(1,0,0;1.5708rad)
  sketch-geometry (8):
    g0: LineSegment StartX=1.9 StartY=12.4688 StartZ=0 EndX=1.9 EndY=8.66879 EndZ=0
    g1: LineSegment StartX=1.9 StartY=8.66879 StartZ=0 EndX=-1.9 EndY=8.66879 EndZ=0
    g2: LineSegment StartX=-1.9 StartY=12.4688 StartZ=0 EndX=-1.9 EndY=8.66879 EndZ=0
    g3: LineSegment StartX=1.9 StartY=12.4688 StartZ=0 EndX=-1.9 EndY=12.4688 EndZ=0
    g4: LineSegment [constr] StartX=-1.9 StartY=12.4688 StartZ=0 EndX=-1.9 EndY=12.6688 EndZ=0
    g5: LineSegment [constr] StartX=-1.9 StartY=12.4688 StartZ=0 EndX=-2.1 EndY=12.4688 EndZ=0
    g6: LineSegment [constr] StartX=1.9 StartY=8.66879 StartZ=0 EndX=2.1 EndY=8.66879 EndZ=0
    g7: LineSegment [constr] StartX=1.9 StartY=8.66879 StartZ=0 EndX=1.9 EndY=8.46879 EndZ=0
  constraints (24):
    c: Coincident(g0,g1)
    c: Coincident(g0,g3)
    c: Coincident(g1,g2)
    c: Coincident(g2,g3)
    c: Coincident(g4,g2)
    c: PointOnObject(g4,g-3)
    c: Vertical(g4)
    c: Distance(g4,g4) = 0.2
    c: Vertical(g2)
    c: Vertical(g0)
    c: Horizontal(g3)
    c: Horizontal(g1)
    c: Coincident(g5,g2)
    c: PointOnObject(g5,g-4)
    c: Horizontal(g5)
    c: Coincident(g6,g0)
    c: PointOnObject(g6,g-6)
    c: Coincident(g7,g0)
    c: PointOnObject(g7,g-5)
    c: Vertical(g7)
    c: Horizontal(g6)
    c: Equal(g6,g7)
    c: Equal(g7,g5)
    c: Equal(g5,g4)
FEATURE [PartDesign::Pad] Pad097
  Direction = (0,-1,0)
  Length = 10
  Length2 = 10
  Offset = -6
  Profile = -> Sketch147
  ReferenceAxis = -> Sketch147 [N_Axis]
  Refine = true
  SideType = 0
  Suppressed = false
  Type = 3
  Type2 = 0
  UpToFace = -> Binder039 [Face9]
FEATURE [Sketcher::SketchObject] Sketch148
  ArcFitTolerance = 1e-06
  AttachmentSupport = -> [Pad097]
  ExternalGeometry = -> [Pad097]
  ExternalTypes = [0,0,0]
  FullyConstrained = true
  MakeInternals = false
  MapMode = 5
  Placement = pos=(0,2.7e-15,12.4688) rot=(0,0,1;0rad)
  sketch-geometry (4):
    g0: LineSegment StartX=-1.9 StartY=-13.5 StartZ=0 EndX=1.9 EndY=-13.5 EndZ=0
    g1: LineSegment StartX=1.9 StartY=-13.5 StartZ=0 EndX=1.9 EndY=-9.7 EndZ=0
    g2: LineSegment StartX=1.9 StartY=-9.7 StartZ=0 EndX=-1.9 EndY=-9.7 EndZ=0
    g3: LineSegment StartX=-1.9 StartY=-9.7 StartZ=0 EndX=-1.9 EndY=-13.5 EndZ=0
  constraints (11):
    c: Coincident(g0,g1)
    c: Coincident(g1,g2)
    c: Coincident(g2,g3)
    c: Coincident(g3,g0)
    c: Horizontal(g0)
    c: Horizontal(g2)
    c: Vertical(g1)
    c: Vertical(g3)
    c: Coincident(g0,g-4)
    c: PointOnObject(g1,g-5)
    c: Equal(g2,g1)
FEATURE [PartDesign::Pad] Pad098
  BaseFeature = -> Pad097
  Direction = (0,0,1)
  Length = 10
  Length2 = 10
  Offset = -6
  Profile = -> Sketch148
  ReferenceAxis = -> Sketch148 [N_Axis]
  Refine = true
  SideType = 0
  Suppressed = false
  Type = 3
  Type2 = 0
  UpToFace = -> Binder039 [Face8]
FEATURE [Sketcher::SketchObject] Sketch149
  ArcFitTolerance = 1e-06
  AttachmentSupport = -> [Pad098]
  ExternalTypes = [0,0,0]
  FullyConstrained = true
  MakeInternals = false
  MapMode = 5
  Placement = pos=(0,-9.7,0) rot=(0,0.707107,0.707107;3.14159rad)
  sketch-geometry (4):
    g0: LineSegment StartX=-1.9 StartY=41.8 StartZ=0 EndX=-1.9 EndY=38 EndZ=0
    g1: LineSegment StartX=-1.9 StartY=38 StartZ=0 EndX=1.9 EndY=38 EndZ=0
    g2: LineSegment StartX=1.9 StartY=38 StartZ=0 EndX=1.9 EndY=41.8 EndZ=0
    g3: LineSegment StartX=1.9 StartY=41.8 StartZ=0 EndX=-1.9 EndY=41.8 EndZ=0
  constraints (11):
    c: Coincident(g0,g1)
    c: Coincident(g1,g2)
    c: Coincident(g2,g3)
    c: Coincident(g3,g0)
    c: Vertical(g0)
    c: Vertical(g2)
    c: Horizontal(g1)
    c: Horizontal(g3)
    c: Coincident(g0,g-4)
    c: PointOnObject(g1,g-5)
    c: Equal(g0,g3)
FEATURE [PartDesign::Pad] Pad099
  BaseFeature = -> Pad098
  Direction = (0,1,-2e-16)
  Length = 8
  Length2 = 10
  Profile = -> Sketch149
  ReferenceAxis = -> Sketch149 [N_Axis]
  Refine = true
  SideType = 0
  Suppressed = false
  Type = 3
  Type2 = 0
  UpToFace = -> XZ_Plane033
FEATURE [Sketcher::SketchObject] Sketch150
  ArcFitTolerance = 1e-06
  AttachmentSupport = -> [Pad099]
  ExternalGeometry = -> [Pad099]
  ExternalTypes = [0,0,0,0]
  FullyConstrained = true
  MakeInternals = false
  MapMode = 5
  Placement = pos=(1.9,5.1055e-12,1.777e-12) rot=(0.57735,0.57735,0.57735;2.0944rad)
  sketch-geometry (4):
    g0: LineSegment StartX=-4 StartY=41.8 StartZ=0 EndX=-4 EndY=38 EndZ=0
    g1: LineSegment StartX=-4 StartY=38 StartZ=0 EndX=-2 EndY=38 EndZ=0
    g2: LineSegment StartX=-2 StartY=38 StartZ=0 EndX=-2 EndY=41.8 EndZ=0
    g3: LineSegment StartX=-2 StartY=41.8 StartZ=0 EndX=-4 EndY=41.8 EndZ=0
  constraints (12):
    c: Coincident(g0,g1)
    c: Coincident(g1,g2)
    c: Coincident(g2,g3)
    c: Coincident(g3,g0)
    c: Vertical(g0)
    c: Vertical(g2)
    c: Horizontal(g1)
    c: Horizontal(g3)
    c: PointOnObject(g2,g-6)
    c: PointOnObject(g1,g-5)
    c: Distance(g3,g3) = 2
    c: Distance(g-6,g2) = 2
FEATURE [PartDesign::Pad] Pad100
  BaseFeature = -> Pad099
  Direction = (1,2.6872e-12,9.353e-13)
  Length = 4
  Length2 = 10
  Profile = -> Sketch150
  ReferenceAxis = -> Sketch150 [N_Axis]
  Refine = true
  SideType = 0
  Suppressed = false
  Type = 0
  Type2 = 0
FEATURE [PartDesign::Fillet] Fillet019
  Base = -> Pad100 [Edge29]
  BaseFeature = -> Pad100
  Radius = 1.5
  Refine = true
  SupportTransform = false
  Suppressed = false
  UseAllEdges = false
FEATURE [Sketcher::SketchObject] Sketch151
  ArcFitTolerance = 1e-06
  AttachmentSupport = -> [Fillet019]
  ExternalGeometry = -> [Fillet019]
  ExternalTypes = [0,0,0,0]
  FullyConstrained = true
  MakeInternals = false
  MapMode = 5
  Placement = pos=(0,-13.5,3.2e-15) rot=(1,0,0;1.5708rad)
  sketch-geometry (4):
    g0: LineSegment StartX=-1.9 StartY=12.4688 StartZ=0 EndX=-1.9 EndY=8.66879 EndZ=0
    g1: LineSegment StartX=-1.9 StartY=8.66879 StartZ=0 EndX=1.9 EndY=8.66879 EndZ=0
    g2: LineSegment StartX=1.9 StartY=8.66879 StartZ=0 EndX=1.9 EndY=12.4688 EndZ=0
    g3: LineSegment StartX=1.9 StartY=12.4688 StartZ=0 EndX=-1.9 EndY=12.4688 EndZ=0
  constraints (10):
    c: Coincident(g0,g1)
    c: Coincident(g1,g2)
    c: Coincident(g2,g3)
    c: Coincident(g3,g0)
    c: Vertical(g0)
    c: Vertical(g2)
    c: Horizontal(g1)
    c: Horizontal(g3)
    c: Coincident(g0,g-3)
    c: Coincident(g1,g-6)
FEATURE [PartDesign::Pad] Pad101
  BaseFeature = -> Fillet019
  Direction = (0,-1,2e-16)
  Length = 4
  Length2 = 10
  Profile = -> Sketch151
  ReferenceAxis = -> Sketch151 [N_Axis]
  Refine = true
  SideType = 0
  Suppressed = false
  Type = 0
  Type2 = 0
FEATURE [Sketcher::SketchObject] Sketch154
  ArcFitTolerance = 1e-06
  AttachmentSupport = -> [Pad101]
  ExternalGeometry = -> [Pad101]
  ExternalTypes = [0,0,0]
  FullyConstrained = true
  MakeInternals = false
  MapMode = 5
  Placement = pos=(0,0,8.66879) rot=(1,0,0;3.14159rad)
  sketch-geometry (4):
    g0: LineSegment StartX=-1.9 StartY=17.5 StartZ=0 EndX=-1.9 EndY=13.7 EndZ=0
    g1: LineSegment StartX=-1.9 StartY=13.7 StartZ=0 EndX=1.9 EndY=13.7 EndZ=0
    g2: LineSegment StartX=1.9 StartY=13.7 StartZ=0 EndX=1.9 EndY=17.5 EndZ=0
    g3: LineSegment StartX=1.9 StartY=17.5 StartZ=0 EndX=-1.9 EndY=17.5 EndZ=0
  constraints (11):
    c: Coincident(g0,g1)
    c: Coincident(g1,g2)
    c: Coincident(g2,g3)
    c: Coincident(g3,g0)
    c: Vertical(g0)
    c: Vertical(g2)
    c: Horizontal(g1)
    c: Horizontal(g3)
    c: Coincident(g0,g-4)
    c: PointOnObject(g1,g-5)
    c: Equal(g2,g3)
FEATURE [PartDesign::Pad] Pad104
  BaseFeature = -> Pad101
  Direction = (0,0,-1)
  Length = 10
  Length2 = 10
  Offset = -8
  Profile = -> Sketch154
  ReferenceAxis = -> Sketch154 [N_Axis]
  Refine = true
  SideType = 0
  Suppressed = false
  Type = 3
  Type2 = 0
  UpToFace = -> Binder039 [Face4]
FEATURE [Sketcher::SketchObject] Sketch153
  ArcFitTolerance = 1e-06
  AttachmentSupport = -> [Pad104]
  ExternalTypes = [0,0,0]
  FullyConstrained = true
  MakeInternals = false
  MapMode = 5
  Placement = pos=(0,-13.7,0) rot=(0,0.707107,0.707107;3.14159rad)
  sketch-geometry (4):
    g0: LineSegment StartX=-1.9 StartY=-11 StartZ=0 EndX=1.9 EndY=-11 EndZ=0
    g1: LineSegment StartX=1.9 StartY=-11 StartZ=0 EndX=1.9 EndY=-7.2 EndZ=0
    g2: LineSegment StartX=1.9 StartY=-7.2 StartZ=0 EndX=-1.9 EndY=-7.2 EndZ=0
    g3: LineSegment StartX=-1.9 StartY=-7.2 StartZ=0 EndX=-1.9 EndY=-11 EndZ=0
  constraints (10):
    c: Coincident(g0,g1)
    c: Coincident(g1,g2)
    c: Coincident(g2,g3)
    c: Coincident(g3,g0)
    c: Horizontal(g2)
    c: Vertical(g1)
    c: Vertical(g3)
    c: Equal(g1,g0)
    c: Coincident(g0,g-5)
    c: Coincident(g0,g-4)
FEATURE [PartDesign::Pad] Pad103
  BaseFeature = -> Pad104
  Direction = (0,1,-2e-16)
  Length = 10
  Length2 = 10
  Profile = -> Sketch153
  ReferenceAxis = -> Sketch153 [N_Axis]
  Refine = true
  SideType = 0
  Suppressed = false
  Type = 3
  Type2 = 0
  UpToFace = -> Pad104 [Face11]
FEATURE [Sketcher::SketchObject] Sketch155
  ArcFitTolerance = 1e-06
  AttachmentSupport = -> [Pad103]
  ExternalGeometry = -> [Pad103]
  ExternalTypes = [0,0,0,0]
  FullyConstrained = true
  MakeInternals = false
  MapMode = 5
  Placement = pos=(1.9,1.1686e-12,1.095e-12) rot=(0.57735,0.57735,0.57735;2.0944rad)
  sketch-geometry (6):
    g0: LineSegment [constr] StartX=-2 StartY=38 StartZ=0 EndX=-2 EndY=-7.2 EndZ=0
    g1: LineSegment [constr] StartX=-4 StartY=38 StartZ=0 EndX=-4 EndY=-7.2 EndZ=0
    g2: LineSegment StartX=-4 StartY=-7.2 StartZ=0 EndX=-4 EndY=-11 EndZ=0
    g3: LineSegment StartX=-4 StartY=-11 StartZ=0 EndX=-2 EndY=-11 EndZ=0
    g4: LineSegment StartX=-2 StartY=-11 StartZ=0 EndX=-2 EndY=-7.2 EndZ=0
    g5: LineSegment StartX=-2 StartY=-7.2 StartZ=0 EndX=-4 EndY=-7.2 EndZ=0
  constraints (16):
    c: Coincident(g0,g-3)
    c: PointOnObject(g0,g-5)
    c: Vertical(g0)
    c: Vertical(g1)
    c: PointOnObject(g1,g-5)
    c: Coincident(g1,g-4)
    c: Coincident(g2,g3)
    c: Coincident(g3,g4)
    c: Coincident(g4,g5)
    c: Coincident(g5,g2)
    c: Vertical(g2)
    c: Vertical(g4)
    c: Horizontal(g3)
    c: Coincident(g2,g1)
    c: PointOnObject(g3,g-6)
    c: Coincident(g4,g0)
FEATURE [PartDesign::Pad] Pad105
  BaseFeature = -> Pad103
  Direction = (1,6.148e-13,5.762e-13)
  Length = 10
  Length2 = 10
  Profile = -> Sketch155
  ReferenceAxis = -> Sketch155 [N_Axis]
  Refine = true
  SideType = 0
  Suppressed = false
  Type = 3
  Type2 = 0
  UpToFace = -> Pad103 [Face16]
FEATURE [PartDesign::Fillet] Fillet020
  Base = -> Pad105 [Edge61]
  BaseFeature = -> Pad105
  Radius = 1.5
  Refine = true
  SupportTransform = false
  Suppressed = false
  UseAllEdges = false
FEATURE [PartDesign::Chamfer] Chamfer004
  Angle = 45
  Base = -> Fillet020 [Edge48,Edge49]
  BaseFeature = -> Fillet020
  ChamferType = 0
  FlipDirection = false
  Refine = true
  Size = 3
  Size2 = 1
  SupportTransform = false
  Suppressed = false
  UseAllEdges = false
FEATURE [PartDesign::Chamfer] Chamfer005
  Angle = 45
  Base = -> Chamfer004 [Edge66]
  BaseFeature = -> Chamfer004
  ChamferType = 0
  FlipDirection = false
  Refine = true
  Size = 0.99
  Size2 = 1
  SupportTransform = false
  Suppressed = false
  UseAllEdges = false
FEATURE [PartDesign::Chamfer] Chamfer006
  Angle = 45
  Base = -> Chamfer005 [Edge44,Edge66]
  BaseFeature = -> Chamfer005
  ChamferType = 0
  FlipDirection = false
  Refine = true
  Size = 3
  Size2 = 1
  SupportTransform = false
  Suppressed = false
  UseAllEdges = false
FEATURE [PartDesign::Body] Body032  label="design6-attachment"
  AllowCompound = false
  Group = -> [Binder038,Binder039,Sketch147,Pad097,Sketch148,Pad098,Sketch149,Pad099,Sketch150,Pad100,Fillet019,Sketch151,Pad101,Sketch153,Sketch154,Pad104,Pad103,Sketch155,Pad105,Fillet020,Chamfer004,Chamfer005,Chamfer006]
  Origin = -> Origin071
  Tip = -> Chamfer006
COMPONENT P26 — recipe-attached ("design6-mirror-attachment-top001", modeled in this document).
Construction recipe (the document's own serialized feature program — sketch geometry with constraints, then the solid features built on it; lengths are millimeters unless a unit is written):

FEATURE [PartDesign::FeatureBase] Clone007
  BaseFeature = -> Pad107
  Suppressed = false
FEATURE [Sketcher::SketchObject] Sketch166
  ArcFitTolerance = 1e-06
  AttachmentSupport = -> [Clone007]
  ExternalGeometry = -> [Pad107]
  ExternalTypes = [0,0]
  FullyConstrained = true
  MakeInternals = false
  MapMode = 5
  Placement = pos=(-2.39779e-11,-1.7849e-12,43.8) rot=(0,0,1;0rad)
  sketch-geometry (4):
    g0: LineSegment StartX=-1.9 StartY=2 StartZ=0 EndX=-1.9 EndY=-2 EndZ=0
    g1: LineSegment StartX=-1.9 StartY=-2 StartZ=0 EndX=1.9 EndY=-2 EndZ=0
    g2: LineSegment StartX=1.9 StartY=-2 StartZ=0 EndX=1.9 EndY=2 EndZ=0
    g3: LineSegment StartX=1.9 StartY=2 StartZ=0 EndX=-1.9 EndY=2 EndZ=0
  constraints (10):
    c: Coincident(g0,g1)
    c: Coincident(g1,g2)
    c: Coincident(g2,g3)
    c: Coincident(g3,g0)
    c: Vertical(g0)
    c: Vertical(g2)
    c: Horizontal(g1)
    c: Horizontal(g3)
    c: Coincident(g0,g-3)
    c: Coincident(g1,g-4)
FEATURE [PartDesign::Pad] Pad112
  BaseFeature = -> Clone007
  Direction = (-5.474e-13,-4.08e-14,1)
  Length = 10
  Length2 = 10
  Profile = -> Sketch166
  ReferenceAxis = -> Sketch166 [N_Axis]
  Refine = true
  SideType = 0
  Suppressed = false
  Type = 0
  Type2 = 0
FEATURE [Sketcher::SketchObject] Sketch165
  ArcFitTolerance = 1e-06
  AttachmentSupport = -> [Pad112]
  ExternalTypes = [0,0,0,0]
  FullyConstrained = true
  MakeInternals = false
  MapMode = 5
  Placement = pos=(-2.94754e-11,-2.1983e-12,53.8) rot=(0,0,1;0rad)
  sketch-geometry (14):
    g0: LineSegment StartX=-0.9 StartY=2 StartZ=0 EndX=-0.9 EndY=-2 EndZ=0
    g1: LineSegment StartX=-0.9 StartY=-2 StartZ=0 EndX=0.9 EndY=-2 EndZ=0
    g2: LineSegment StartX=0.9 StartY=-2 StartZ=0 EndX=0.9 EndY=2 EndZ=0
    g3: LineSegment StartX=0.9 StartY=2 StartZ=0 EndX=-0.9 EndY=2 EndZ=0
    g4: LineSegment StartX=-1.4 StartY=-2 StartZ=0 EndX=-1.4 EndY=2 EndZ=0
    g5: LineSegment StartX=-1.4 StartY=2 StartZ=0 EndX=-2 EndY=2 EndZ=0
    g6: LineSegment StartX=-2 StartY=2 StartZ=0 EndX=-2 EndY=-2 EndZ=0
    g7: LineSegment StartX=-2 StartY=-2 StartZ=0 EndX=-1.4 EndY=-2 EndZ=0
    g8: LineSegment [constr] StartX=-0.9 StartY=2 StartZ=0 EndX=-1.4 EndY=2 EndZ=0
    g9: LineSegment StartX=1.4 StartY=-2 StartZ=0 EndX=2 EndY=-2 EndZ=0
    g10: LineSegment StartX=2 StartY=-2 StartZ=0 EndX=2 EndY=2 EndZ=0
    g11: LineSegment StartX=2 StartY=2 StartZ=0 EndX=1.4 EndY=2 EndZ=0
    g12: LineSegment StartX=1.4 StartY=2 StartZ=0 EndX=1.4 EndY=-2 EndZ=0
    g13: LineSegment [constr] StartX=0.9 StartY=2 StartZ=0 EndX=1.4 EndY=2 EndZ=0
  constraints (36):
    c: Coincident(g0,g1)
    c: Coincident(g1,g2)
    c: Coincident(g2,g3)
    c: Coincident(g3,g0)
    c: Vertical(g0)
    c: Vertical(g2)
    c: Horizontal(g1)
    c: Horizontal(g3)
    c: Symmetric(g0,g1,g-1)
    c: Distance(g3,g3) = 1.8
    c: Coincident(g4,g5)
    c: Coincident(g5,g6)
    c: Coincident(g6,g7)
    c: Coincident(g7,g4)
    c: Vertical(g4)
    c: Horizontal(g5)
    c: Horizontal(g7)
    c: Coincident(g8,g0)
    c: Coincident(g8,g4)
    c: Horizontal(g8)
    c: Distance(g4,g0) = 0.5
    c: Coincident(g9,g10)
    c: Coincident(g10,g11)
    c: Coincident(g11,g12)
    c: Coincident(g12,g9)
    c: Horizontal(g9)
    c: Horizontal(g11)
    c: Vertical(g10)
    c: Vertical(g12)
    c: Equal(g11,g5)
    c: Coincident(g13,g2)
    c: Coincident(g13,g11)
    c: Horizontal(g13)
    c: Coincident(g5,g-4)
    c: Coincident(g6,g-3)
    c: Coincident(g9,g-5)
FEATURE [PartDesign::Pocket] Pocket033
  BaseFeature = -> Pad112
  Direction = (5.479e-13,4.09e-14,-1)
  Length = 2
  Length2 = 5
  Profile = -> Sketch165
  ReferenceAxis = -> Sketch165 [N_Axis]
  Refine = true
  SideType = 0
  Suppressed = false
  Type = 0
  Type2 = 0
FEATURE [PartDesign::Fillet] Fillet022
  Base = -> Pocket033 [Edge70,Edge63]
  BaseFeature = -> Pocket033
  Radius = 0.49
  Refine = true
  SupportTransform = false
  Suppressed = false
  UseAllEdges = false
FEATURE [PartDesign::Body] Body035  label="design6-mirror-attachment-top"
  AllowCompound = false
  Group = -> [Clone007,Sketch166,Sketch165,Pad112,Pocket033,Fillet022]
  Origin = -> Origin077
  Tip = -> Fillet022
COMPONENT P27 — recipe-attached ("design6-mirror-attachment-bottom001", modeled in this document).
Construction recipe (the document's own serialized feature program — sketch geometry with constraints, then the solid features built on it; lengths are millimeters unless a unit is written):

FEATURE [PartDesign::FeatureBase] Clone008
  BaseFeature = -> Mirror009
  Placement = pos=(0,0,-0.7554) rot=(0,0,1;0rad)
  Suppressed = false
FEATURE [Sketcher::SketchObject] Sketch167
  ArcFitTolerance = 1e-06
  AttachmentSupport = -> [Clone008]
  ExternalGeometry = -> [Clone008]
  ExternalTypes = [0,0]
  FullyConstrained = true
  MakeInternals = false
  MapMode = 5
  Placement = pos=(6.7048e-12,-4.99e-13,11.4892) rot=(0,0,1;0rad)
  sketch-geometry (4):
    g0: LineSegment StartX=-1.9 StartY=-2 StartZ=0 EndX=1.9 EndY=-2 EndZ=0
    g1: LineSegment StartX=1.9 StartY=-2 StartZ=0 EndX=1.9 EndY=2 EndZ=0
    g2: LineSegment StartX=1.9 StartY=2 StartZ=0 EndX=-1.9 EndY=2 EndZ=0
    g3: LineSegment StartX=-1.9 StartY=2 StartZ=0 EndX=-1.9 EndY=-2 EndZ=0
  constraints (10):
    c: Coincident(g0,g1)
    c: Coincident(g1,g2)
    c: Coincident(g2,g3)
    c: Coincident(g3,g0)
    c: Horizontal(g0)
    c: Horizontal(g2)
    c: Vertical(g1)
    c: Vertical(g3)
    c: Coincident(g0,g-4)
    c: Coincident(g1,g-3)
FEATURE [PartDesign::Pad] Pad113
  BaseFeature = -> Clone008
  Direction = (5.476e-13,-4.08e-14,1)
  Length = 2
  Length2 = 10
  Placement = pos=(0,0,-0.7554) rot=(0,0,1;0rad)
  Profile = -> Sketch167
  ReferenceAxis = -> Sketch167 [N_Axis]
  Refine = true
  SideType = 0
  Suppressed = false
  Type = 0
  Type2 = 0
FEATURE [Sketcher::SketchObject] Sketch168
  ArcFitTolerance = 1e-06
  AttachmentSupport = -> [Pad113]
  ExternalGeometry = -> [Pad113]
  ExternalTypes = [0,0,0]
  FullyConstrained = true
  MakeInternals = false
  MapMode = 5
  Placement = pos=(7.8042e-12,-5.82e-13,13.4892) rot=(0,0,1;0rad)
  sketch-geometry (12):
    g0: LineSegment StartX=-1.9 StartY=0.9 StartZ=0 EndX=-1.9 EndY=-0.9 EndZ=0
    g1: LineSegment StartX=-1.9 StartY=-0.9 StartZ=0 EndX=1.9 EndY=-0.9 EndZ=0
    g2: LineSegment StartX=1.9 StartY=-0.9 StartZ=0 EndX=1.9 EndY=0.9 EndZ=0
    g3: LineSegment StartX=1.9 StartY=0.9 StartZ=0 EndX=-1.9 EndY=0.9 EndZ=0
    g4: LineSegment StartX=-1.9 StartY=2 StartZ=0 EndX=-1.9 EndY=1.4 EndZ=0
    g5: LineSegment StartX=-1.9 StartY=1.4 StartZ=0 EndX=1.9 EndY=1.4 EndZ=0
    g6: LineSegment StartX=1.9 StartY=1.4 StartZ=0 EndX=1.9 EndY=2 EndZ=0
    g7: LineSegment StartX=1.9 StartY=2 StartZ=0 EndX=-1.9 EndY=2 EndZ=0
    g8: LineSegment StartX=-1.9 StartY=-2 StartZ=0 EndX=1.9 EndY=-2 EndZ=0
    g9: LineSegment StartX=1.9 StartY=-2 StartZ=0 EndX=1.9 EndY=-1.4 EndZ=0
    g10: LineSegment StartX=1.9 StartY=-1.4 StartZ=0 EndX=-1.9 EndY=-1.4 EndZ=0
    g11: LineSegment StartX=-1.9 StartY=-1.4 StartZ=0 EndX=-1.9 EndY=-2 EndZ=0
  constraints (33):
    c: Coincident(g0,g1)
    c: Vertical(g0)
    c: Vertical(g2)
    c: Horizontal(g1)
    c: Symmetric(g1,g0,g-1)
    c: Coincident(g0,g3)
    c: Coincident(g2,g3)
    c: Horizontal(g3)
    c: Coincident(g1,g2)
    c: PointOnObject(g1,g-5)
    c: Distance(g2,g2) = 1.8
    c: Coincident(g4,g5)
    c: Coincident(g5,g6)
    c: Coincident(g6,g7)
    c: Coincident(g7,g4)
    c: Vertical(g4)
    c: Vertical(g6)
    c: Horizontal(g5)
    c: Horizontal(g7)
    c: Coincident(g4,g-4)
    c: PointOnObject(g5,g-5)
    c: Distance(g5,g3) = 0.5
    c: Coincident(g8,g9)
    c: Coincident(g9,g10)
    c: Coincident(g10,g11)
    c: Coincident(g11,g8)
    c: Horizontal(g8)
    c: Horizontal(g10)
    c: Vertical(g9)
    c: Vertical(g11)
    c: Coincident(g8,g-3)
    c: PointOnObject(g9,g-5)
    c: Distance(g9,g1) = 0.5
FEATURE [PartDesign::Pocket] Pocket034
  BaseFeature = -> Pad113
  Direction = (-5.479e-13,4.09e-14,-1)
  Length = 2
  Length2 = 5
  Placement = pos=(0,0,-0.7554) rot=(0,0,1;0rad)
  Profile = -> Sketch168
  ReferenceAxis = -> Sketch168 [N_Axis]
  Refine = true
  SideType = 0
  Suppressed = false
  Type = 0
  Type2 = 0
FEATURE [PartDesign::Fillet] Fillet023
  Base = -> Pocket034 [Edge68,Edge74]
  BaseFeature = -> Pocket034
  Placement = pos=(0,0,-0.7554) rot=(0,0,1;0rad)
  Radius = 0.59
  Refine = true
  SupportTransform = false
  Suppressed = false
  UseAllEdges = false
FEATURE [PartDesign::Body] Body036  label="design6-mirror-attachment-bottom"
  AllowCompound = false
  Group = -> [Clone008,Sketch167,Pad113,Sketch168,Pocket034,Fillet023]
  Origin = -> Origin079
  Tip = -> Fillet023
COMPONENT P28 — recipe-attached ("design6-stator001", modeled in this document).
Construction recipe (the document's own serialized feature program — sketch geometry with constraints, then the solid features built on it; lengths are millimeters unless a unit is written):

FEATURE [PartDesign::SubShapeBinder] Binder034
  BindCopyOnChange = 0
  BindMode = 0
  ClaimChildren = false
  Context = -> Body028 [Binder034.]
  Fuse = false
  MakeFace = true
  OffsetFill = false
  OffsetIntersection = false
  OffsetJoinType = 0
  OffsetOpenResult = false
  PartialLoad = false
  Refine = true
  Relative = true
  Support = -> [Body029]
  _Version = 2
FEATURE [Sketcher::SketchObject] Sketch131
  ArcFitTolerance = 1e-06
  AttachmentSupport = -> [Binder034]
  ExternalGeometry = -> [Binder034]
  ExternalTypes = [0]
  FullyConstrained = true
  MakeInternals = false
  MapMode = 5
  Placement = pos=(0,0,0) rot=(1,0,0;3.14159rad)
  sketch-geometry (1):
    g0: Circle CenterX=0 CenterY=0 CenterZ=0 NormalX=0 NormalY=0 NormalZ=1 AngleXU=0 Radius=2.6
  constraints (2):
    c: Coincident(g0,g-3)
    c: Distance(g-3,g0) = 0.1
FEATURE [PartDesign::Pad] Pad085
  Direction = (0,0,-1)
  Length = 10
  Length2 = 10
  Profile = -> Sketch131
  ReferenceAxis = -> Sketch131 [N_Axis]
  Refine = true
  Reversed = true
  SideType = 0
  Suppressed = false
  Type = 3
  Type2 = 0
  UpToFace = -> Binder034 [Face3]
FEATURE [Sketcher::SketchObject] Sketch132
  ArcFitTolerance = 1e-06
  AttachmentSupport = -> [Pad085]
  ExternalTypes = [0]
  FullyConstrained = true
  MakeInternals = false
  MapMode = 5
  Placement = pos=(0,0,0) rot=(1,0,0;3.14159rad)
  sketch-geometry (1):
    g0: Circle CenterX=0 CenterY=0 CenterZ=0 NormalX=0 NormalY=0 NormalZ=1 AngleXU=0 Radius=3.25
  constraints (2):
    c: Diameter(g0) = 6.5
    c: Coincident(g0,g-1)
FEATURE [PartDesign::Pad] Pad086
  BaseFeature = -> Pad085
  Direction = (0,0,-1)
  Length = 1
  Length2 = 10
  Profile = -> Sketch132
  ReferenceAxis = -> Sketch132 [N_Axis]
  Refine = true
  SideType = 0
  Suppressed = false
  Type = 0
  Type2 = 0
FEATURE [Sketcher::SketchObject] Sketch133
  ArcFitTolerance = 1e-06
  AttachmentSupport = -> [Pad086]
  ExternalTypes = [0]
  FullyConstrained = true
  MakeInternals = false
  MapMode = 5
  Placement = pos=(0,0,-1) rot=(1,0,0;3.14159rad)
  sketch-geometry (1):
    g0: Circle CenterX=0 CenterY=0 CenterZ=0 NormalX=0 NormalY=0 NormalZ=1 AngleXU=0 Radius=9
  constraints (2):
    c: Diameter(g0) = 18
    c: Coincident(g0,g-1)
FEATURE [PartDesign::Pad] Pad087
  BaseFeature = -> Pad086
  Direction = (0,0,-1)
  Length = 2
  Length2 = 10
  Profile = -> Sketch133
  ReferenceAxis = -> Sketch133 [N_Axis]
  Refine = true
  SideType = 0
  Suppressed = false
  Type = 0
  Type2 = 0
FEATURE [PartDesign::Chamfer] Chamfer003
  Angle = 45
  Base = -> Pad087 [Edge6]
  BaseFeature = -> Pad087
  ChamferType = 0
  FlipDirection = false
  Refine = true
  Size = 0.99
  Size2 = 1
  SupportTransform = false
  Suppressed = false
  UseAllEdges = false
FEATURE [PartDesign::Body] Body028  label="design6-stator"
  AllowCompound = false
  Group = -> [Binder034,Sketch131,Pad085,Sketch132,Pad086,Sketch133,Pad087,Chamfer003]
  Origin = -> Origin063
  Tip = -> Chamfer003
COMPONENT P29 — recipe-attached ("small_bearing001", modeled in this document).
Construction recipe (the document's own serialized feature program — sketch geometry with constraints, then the solid features built on it; lengths are millimeters unless a unit is written):

FEATURE [Sketcher::SketchObject] Sketch129
  ArcFitTolerance = 1e-06
  AttachmentSupport = -> [Origin065]
  ExternalTypes = [0]
  FullyConstrained = true
  MakeInternals = false
  MapMode = 5
  sketch-geometry (1):
    g0: Circle CenterX=0 CenterY=0 CenterZ=0 NormalX=0 NormalY=0 NormalZ=1 AngleXU=0 Radius=5.5
  constraints (2):
    c: Diameter(g0) = 11
    c: Coincident(g0,g-1)
FEATURE [PartDesign::Pad] Pad084
  Direction = (0,0,1)
  Length = 3
  Length2 = 10
  Profile = -> Sketch129
  ReferenceAxis = -> Sketch129 [N_Axis]
  Refine = true
  SideType = 0
  Suppressed = false
  Type = 0
  Type2 = 0
FEATURE [Sketcher::SketchObject] Sketch130
  ArcFitTolerance = 1e-06
  AttachmentSupport = -> [Pad084]
  ExternalTypes = [0]
  FullyConstrained = true
  MakeInternals = false
  MapMode = 5
  Placement = pos=(0,0,3) rot=(0,0,1;0rad)
  sketch-geometry (1):
    g0: Circle CenterX=0 CenterY=0 CenterZ=0 NormalX=0 NormalY=0 NormalZ=1 AngleXU=0 Radius=2.5
  constraints (2):
    c: Diameter(g0) = 5
    c: Coincident(g0,g-1)
FEATURE [PartDesign::Pocket] Pocket029
  BaseFeature = -> Pad084
  Direction = (0,0,-1)
  Length = 5
  Length2 = 5
  Profile = -> Sketch130
  ReferenceAxis = -> Sketch130 [N_Axis]
  Refine = true
  SideType = 0
  Suppressed = false
  Type = 1
  Type2 = 0
FEATURE [PartDesign::Body] Body029  label="small_bearing"
  AllowCompound = false
  Group = -> [Sketch129,Pad084,Sketch130,Pocket029]
  Origin = -> Origin065
  Tip = -> Pocket029
COMPONENT P30 — same part as P25; its construction recipe is shown at P25.
PROVENANCE & LICENSES
A FreeCAD (.FCStd) document from a public repository crawl; recipes are the document's own serialized feature recipes (and, for linked parts, companion documents' recipes).
License: as declared in the source repository (recorded in the dataset sidecar).
